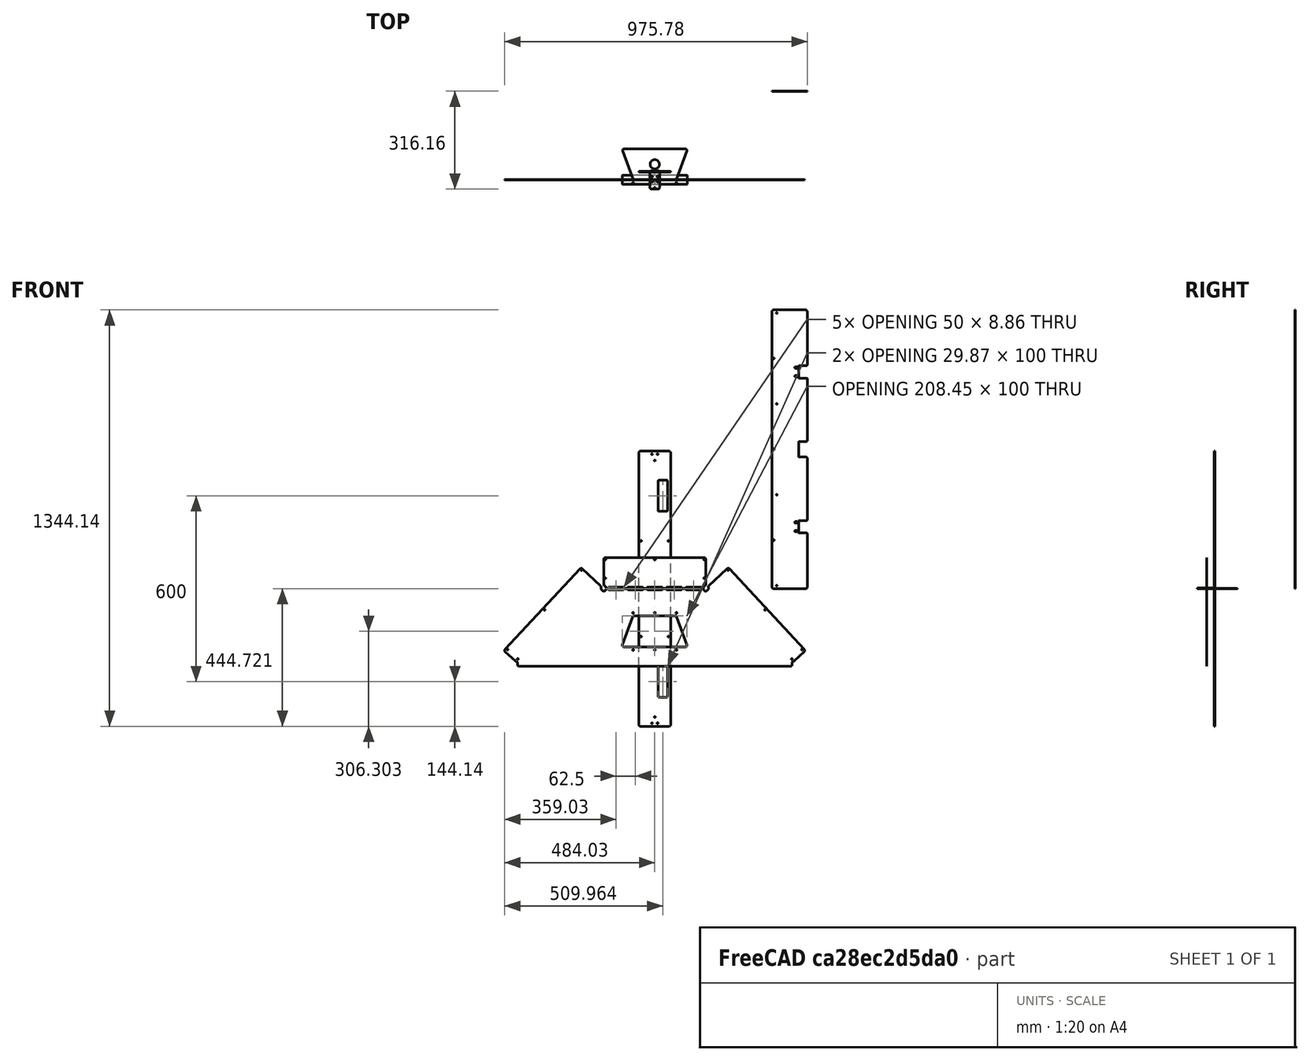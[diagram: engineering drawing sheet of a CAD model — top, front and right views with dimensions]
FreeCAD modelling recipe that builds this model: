
FCSTD DOCUMENT  (FreeCAD 0.22R38622 (Git))
Label: composit_stand12_ss
License: All rights reserved
LicenseURL: http://en.wikipedia.org/wiki/All_rights_reserved
objects: Sketcher::SketchObject×22, TechDraw::DrawViewDimension×16, TechDraw::DrawProjGroupItem×8, App::DocumentObjectGroup×8, Part::Feature×6, App::Link×5, TechDraw::DrawSVGTemplate×4, TechDraw::DrawPage×4, TechDraw::DrawViewBalloon×2
note: 80 computed .brp shape members not serialized (recipe doc carries the construction recipe); baked Part::Feature solids carry a one-line shape summary decoded from their .brp
EXTERNAL_REF file=composit_stand12.FCStd obj=Body008
EXTERNAL_REF file=composit_stand12.FCStd obj=Body002
EXTERNAL_REF file=composit_stand12.FCStd obj=Body006
EXTERNAL_REF file=composit_stand12.FCStd obj=Body018
EXTERNAL_REF file=composit_stand12.FCStd obj=Body019

FEATURE [App::Link] Link001  label="bar_fix"
  LinkedObject = -> <external composit_stand12.FCStd>#Body008
FEATURE [App::Link] Link002  label="sink"
  LinkedObject = -> <external composit_stand12.FCStd>#Body002
FEATURE [App::Link] Link003  label="bar"
  LinkedObject = -> <external composit_stand12.FCStd>#Body006
FEATURE [Part::Feature] Unfold
  shape: bbox 102.3 x 3.402 x 888.3 mm, 40 faces (baked)
FEATURE [Sketcher::SketchObject] Unfold_Sketch_Outline
  ArcFitTolerance = 0
  FullyConstrained = false
  MakeInternals = false
  sketch-geometry (8):
    g0: LineSegment StartX=-444.137 StartY=-46.1681 StartZ=0 EndX=-444.137 EndY=46.1681 EndZ=0
    g1: ArcOfCircle CenterX=-439.137 CenterY=46.1681 CenterZ=0 NormalX=0 NormalY=0 NormalZ=1 AngleXU=1.5708 Radius=5 StartAngle=0 EndAngle=1.5708
    g2: LineSegment StartX=439.137 StartY=51.1681 StartZ=0 EndX=-439.137 EndY=51.1681 EndZ=0
    g3: ArcOfCircle CenterX=439.137 CenterY=46.1681 CenterZ=0 NormalX=0 NormalY=0 NormalZ=1 AngleXU=1.5708 Radius=5 StartAngle=4.71239 EndAngle=6.28319
    g4: LineSegment StartX=444.137 StartY=-46.1681 StartZ=0 EndX=444.137 EndY=46.1681 EndZ=0
    g5: ArcOfCircle CenterX=439.137 CenterY=-46.1681 CenterZ=0 NormalX=0 NormalY=0 NormalZ=1 AngleXU=-1.5708 Radius=5 StartAngle=2e-16 EndAngle=1.5708
    g6: LineSegment StartX=439.137 StartY=-51.1681 StartZ=0 EndX=-439.137 EndY=-51.1681 EndZ=0
    g7: ArcOfCircle CenterX=-439.137 CenterY=-46.1681 CenterZ=0 NormalX=0 NormalY=0 NormalZ=1 AngleXU=-1.5708 Radius=5 StartAngle=4.71239 EndAngle=6.28319
FEATURE [Sketcher::SketchObject] Unfold_Sketch_Internal
  ArcFitTolerance = 0
  FullyConstrained = false
  MakeInternals = false
  sketch-geometry (30):
    g0: ArcOfCircle CenterX=252 CenterY=38.8681 CenterZ=0 NormalX=0 NormalY=0 NormalZ=1 AngleXU=1.5708 Radius=2 StartAngle=4e-16 EndAngle=0.863212
    g1: BSplineCurve PolesCount=15 KnotsCount=13 Degree=3 IsPeriodic=0
    g2: LineSegment StartX=250 StartY=13 StartZ=0 EndX=250 EndY=39.3075 EndZ=0
    g3: ArcOfCircle CenterX=252 CenterY=13 CenterZ=0 NormalX=0 NormalY=0 NormalZ=1 AngleXU=1.5708 Radius=2 StartAngle=1.5708 EndAngle=3.14159
    g4: LineSegment StartX=348 StartY=11 StartZ=0 EndX=252 EndY=11 EndZ=0
    g5: ArcOfCircle CenterX=348 CenterY=13 CenterZ=0 NormalX=0 NormalY=0 NormalZ=1 AngleXU=1.5708 Radius=2 StartAngle=3.14159 EndAngle=4.71239
    g6: LineSegment StartX=350 StartY=39.3075 StartZ=0 EndX=350 EndY=13 EndZ=0
    g7: BSplineCurve PolesCount=15 KnotsCount=13 Degree=3 IsPeriodic=0
    g8: ArcOfCircle CenterX=348 CenterY=38.8681 CenterZ=0 NormalX=0 NormalY=0 NormalZ=1 AngleXU=1.5708 Radius=2 StartAngle=5.41997 EndAngle=6.28319
    g9: LineSegment StartX=348 StartY=40.8681 StartZ=0 EndX=252 EndY=40.8681 EndZ=0
    g10: LineSegment StartX=-350 StartY=13 StartZ=0 EndX=-350 EndY=39.3075 EndZ=0
    g11: BSplineCurve PolesCount=15 KnotsCount=13 Degree=3 IsPeriodic=0
    g12: ArcOfCircle CenterX=-348 CenterY=38.8681 CenterZ=0 NormalX=0 NormalY=0 NormalZ=1 AngleXU=1.5708 Radius=2 StartAngle=4e-16 EndAngle=0.863212
    g13: LineSegment StartX=-252 StartY=40.8681 StartZ=0 EndX=-348 EndY=40.8681 EndZ=0
    g14: ArcOfCircle CenterX=-252 CenterY=38.8681 CenterZ=0 NormalX=0 NormalY=0 NormalZ=1 AngleXU=1.5708 Radius=2 StartAngle=5.41997 EndAngle=6.28319
    g15: BSplineCurve PolesCount=15 KnotsCount=13 Degree=3 IsPeriodic=0
    g16: LineSegment StartX=-250 StartY=13 StartZ=0 EndX=-250 EndY=39.3075 EndZ=0
    g17: ArcOfCircle CenterX=-252 CenterY=13 CenterZ=0 NormalX=0 NormalY=0 NormalZ=1 AngleXU=1.5708 Radius=2 StartAngle=3.14159 EndAngle=4.71239
    g18: LineSegment StartX=-252 StartY=11 StartZ=0 EndX=-348 EndY=11 EndZ=0
    g19: ArcOfCircle CenterX=-348 CenterY=13 CenterZ=0 NormalX=0 NormalY=0 NormalZ=1 AngleXU=1.5708 Radius=2 StartAngle=1.5708 EndAngle=3.14159
    g20: Circle CenterX=414.137 CenterY=0 CenterZ=0 NormalX=0 NormalY=0 NormalZ=-1 AngleXU=-1.5708 Radius=1.7
    g21: Circle CenterX=-414.137 CenterY=0 CenterZ=0 NormalX=0 NormalY=0 NormalZ=-1 AngleXU=1.5708 Radius=1.7
    g22: Circle CenterX=434.137 CenterY=9 CenterZ=0 NormalX=0 NormalY=0 NormalZ=-1 AngleXU=-1.5708 Radius=1.7
    g23: Circle CenterX=-434.137 CenterY=9 CenterZ=0 NormalX=0 NormalY=0 NormalZ=-1 AngleXU=1.5708 Radius=1.7
    g24: Circle CenterX=434.137 CenterY=-9 CenterZ=0 NormalX=0 NormalY=0 NormalZ=-1 AngleXU=-1.5708 Radius=1.7
    g25: Circle CenterX=-434.137 CenterY=-9 CenterZ=0 NormalX=0 NormalY=0 NormalZ=-1 AngleXU=1.5708 Radius=1.7
    g26: Circle CenterX=154.5 CenterY=-44.1681 CenterZ=0 NormalX=0 NormalY=0 NormalZ=1 AngleXU=-3.14159 Radius=1.7
    g27: Circle CenterX=-154.5 CenterY=-44.1681 CenterZ=0 NormalX=0 NormalY=0 NormalZ=1 AngleXU=-3.14159 Radius=1.7
    g28: Circle CenterX=154.5 CenterY=44.1681 CenterZ=0 NormalX=0 NormalY=0 NormalZ=1 AngleXU=-3.14159 Radius=1.7
    g29: Circle CenterX=-154.5 CenterY=44.1681 CenterZ=0 NormalX=0 NormalY=0 NormalZ=1 AngleXU=-3.14159 Radius=1.7
FEATURE [Sketcher::SketchObject] Unfold_Sketch_bends
  ArcFitTolerance = 0
  FullyConstrained = false
  MakeInternals = false
  sketch-geometry (8):
    g0: LineSegment StartX=-444.137 StartY=15.042 StartZ=0 EndX=-350 EndY=15.042 EndZ=0
    g1: LineSegment StartX=-444.137 StartY=38.1261 StartZ=0 EndX=-350 EndY=38.1261 EndZ=0
    g2: LineSegment StartX=-250 StartY=15.042 StartZ=0 EndX=250 EndY=15.042 EndZ=0
    g3: LineSegment StartX=-250 StartY=38.1261 StartZ=0 EndX=250 EndY=38.1261 EndZ=0
    g4: LineSegment StartX=350 StartY=38.1261 StartZ=0 EndX=444.137 EndY=38.1261 EndZ=0
    g5: LineSegment StartX=350 StartY=15.042 StartZ=0 EndX=444.137 EndY=15.042 EndZ=0
    g6: LineSegment StartX=-444.137 StartY=-38.1261 StartZ=0 EndX=444.137 EndY=-38.1261 EndZ=0
    g7: LineSegment StartX=-444.137 StartY=-15.042 StartZ=0 EndX=444.137 EndY=-15.042 EndZ=0
FEATURE [Sketcher::SketchObject] Unfold_Sketch
  ArcFitTolerance = 0
  ExternalGeometry = -> [Unfold_Sketch_bends]
  FullyConstrained = false
  MakeInternals = false
  sketch-geometry (46):
    g0: LineSegment StartX=-444.137 StartY=-46.1681 StartZ=0 EndX=-444.137 EndY=46.1681 EndZ=0
    g1: ArcOfCircle CenterX=-439.137 CenterY=-46.1681 CenterZ=0 NormalX=0 NormalY=0 NormalZ=1 AngleXU=-1.5708 Radius=5 StartAngle=4.71239 EndAngle=6.28319
    g2: LineSegment StartX=439.137 StartY=-51.1681 StartZ=0 EndX=-439.137 EndY=-51.1681 EndZ=0
    g3: ArcOfCircle CenterX=439.137 CenterY=-46.1681 CenterZ=0 NormalX=0 NormalY=0 NormalZ=1 AngleXU=-1.5708 Radius=5 StartAngle=2e-16 EndAngle=1.5708
    g4: LineSegment StartX=444.137 StartY=-46.1681 StartZ=0 EndX=444.137 EndY=46.1681 EndZ=0
    g5: ArcOfCircle CenterX=439.137 CenterY=46.1681 CenterZ=0 NormalX=0 NormalY=0 NormalZ=1 AngleXU=1.5708 Radius=5 StartAngle=4.71239 EndAngle=6.28319
    g6: LineSegment StartX=439.137 StartY=51.1681 StartZ=0 EndX=-439.137 EndY=51.1681 EndZ=0
    g7: ArcOfCircle CenterX=-439.137 CenterY=46.1681 CenterZ=0 NormalX=0 NormalY=0 NormalZ=1 AngleXU=1.5708 Radius=5 StartAngle=0 EndAngle=1.5708
    g8: LineSegment StartX=-350 StartY=13 StartZ=0 EndX=-350 EndY=39.3075 EndZ=0
    g9: BSplineCurve PolesCount=15 KnotsCount=13 Degree=3 IsPeriodic=0
    g10: ArcOfCircle CenterX=-348 CenterY=38.8681 CenterZ=0 NormalX=0 NormalY=0 NormalZ=1 AngleXU=1.5708 Radius=2 StartAngle=4e-16 EndAngle=0.863212
    g11: LineSegment StartX=-252 StartY=40.8681 StartZ=0 EndX=-348 EndY=40.8681 EndZ=0
    g12: ArcOfCircle CenterX=-252 CenterY=38.8681 CenterZ=0 NormalX=0 NormalY=0 NormalZ=1 AngleXU=1.5708 Radius=2 StartAngle=5.41997 EndAngle=6.28319
    g13: BSplineCurve PolesCount=15 KnotsCount=13 Degree=3 IsPeriodic=0
    g14: LineSegment StartX=-250 StartY=13 StartZ=0 EndX=-250 EndY=39.3075 EndZ=0
    g15: ArcOfCircle CenterX=-252 CenterY=13 CenterZ=0 NormalX=0 NormalY=0 NormalZ=1 AngleXU=1.5708 Radius=2 StartAngle=3.14159 EndAngle=4.71239
    g16: LineSegment StartX=-252 StartY=11 StartZ=0 EndX=-348 EndY=11 EndZ=0
    g17: ArcOfCircle CenterX=-348 CenterY=13 CenterZ=0 NormalX=0 NormalY=0 NormalZ=1 AngleXU=1.5708 Radius=2 StartAngle=1.5708 EndAngle=3.14159
    g18: ArcOfCircle CenterX=252 CenterY=38.8681 CenterZ=0 NormalX=0 NormalY=0 NormalZ=1 AngleXU=1.5708 Radius=2 StartAngle=4e-16 EndAngle=0.863212
    g19: LineSegment StartX=348 StartY=40.8681 StartZ=0 EndX=252 EndY=40.8681 EndZ=0
    g20: ArcOfCircle CenterX=348 CenterY=38.8681 CenterZ=0 NormalX=0 NormalY=0 NormalZ=1 AngleXU=1.5708 Radius=2 StartAngle=5.41997 EndAngle=6.28319
    g21: BSplineCurve PolesCount=15 KnotsCount=13 Degree=3 IsPeriodic=0
    g22: LineSegment StartX=350 StartY=39.3075 StartZ=0 EndX=350 EndY=13 EndZ=0
    g23: ArcOfCircle CenterX=348 CenterY=13 CenterZ=0 NormalX=0 NormalY=0 NormalZ=1 AngleXU=1.5708 Radius=2 StartAngle=3.14159 EndAngle=4.71239
    g24: LineSegment StartX=348 StartY=11 StartZ=0 EndX=252 EndY=11 EndZ=0
    g25: ArcOfCircle CenterX=252 CenterY=13 CenterZ=0 NormalX=0 NormalY=0 NormalZ=1 AngleXU=1.5708 Radius=2 StartAngle=1.5708 EndAngle=3.14159
    g26: LineSegment StartX=250 StartY=13 StartZ=0 EndX=250 EndY=39.3075 EndZ=0
    g27: BSplineCurve PolesCount=15 KnotsCount=13 Degree=3 IsPeriodic=0
    g28: Circle CenterX=-154.5 CenterY=44.1681 CenterZ=0 NormalX=0 NormalY=0 NormalZ=1 AngleXU=-3.14159 Radius=1.7
    g29: Circle CenterX=154.5 CenterY=44.1681 CenterZ=0 NormalX=0 NormalY=0 NormalZ=1 AngleXU=-3.14159 Radius=1.7
    g30: Circle CenterX=-154.5 CenterY=-44.1681 CenterZ=0 NormalX=0 NormalY=0 NormalZ=1 AngleXU=-3.14159 Radius=1.7
    g31: Circle CenterX=154.5 CenterY=-44.1681 CenterZ=0 NormalX=0 NormalY=0 NormalZ=1 AngleXU=-3.14159 Radius=1.7
    g32: Circle CenterX=-434.137 CenterY=-9 CenterZ=0 NormalX=0 NormalY=0 NormalZ=-1 AngleXU=1.5708 Radius=1.7
    g33: Circle CenterX=434.137 CenterY=-9 CenterZ=0 NormalX=0 NormalY=0 NormalZ=-1 AngleXU=-1.5708 Radius=1.7
    g34: Circle CenterX=-414.137 CenterY=0 CenterZ=0 NormalX=0 NormalY=0 NormalZ=-1 AngleXU=1.5708 Radius=1.7
    g35: Circle CenterX=-434.137 CenterY=9 CenterZ=0 NormalX=0 NormalY=0 NormalZ=-1 AngleXU=1.5708 Radius=1.7
    g36: Circle CenterX=414.137 CenterY=0 CenterZ=0 NormalX=0 NormalY=0 NormalZ=-1 AngleXU=-1.5708 Radius=1.7
    g37: Circle CenterX=434.137 CenterY=9 CenterZ=0 NormalX=0 NormalY=0 NormalZ=-1 AngleXU=-1.5708 Radius=1.7
    g38: LineSegment StartX=444.137 StartY=38.1261 StartZ=0 EndX=442.137 EndY=38.1261 EndZ=0
    g39: LineSegment StartX=444.137 StartY=15.042 StartZ=0 EndX=442.137 EndY=15.042 EndZ=0
    g40: LineSegment StartX=444.137 StartY=-15.042 StartZ=0 EndX=442.137 EndY=-15.042 EndZ=0
    g41: LineSegment StartX=444.137 StartY=-38.1261 StartZ=0 EndX=442.137 EndY=-38.1261 EndZ=0
    g42: LineSegment StartX=-444.137 StartY=-38.1261 StartZ=0 EndX=-442.137 EndY=-38.1261 EndZ=0
    g43: LineSegment StartX=-444.137 StartY=-15.042 StartZ=0 EndX=-442.137 EndY=-15.042 EndZ=0
    g44: LineSegment StartX=-444.137 StartY=15.042 StartZ=0 EndX=-442.137 EndY=15.042 EndZ=0
    g45: LineSegment StartX=-444.137 StartY=38.1261 StartZ=0 EndX=-442.137 EndY=38.1261 EndZ=0
  constraints (24):
    c: Coincident(g38,g-8)
    c: PointOnObject(g38,g-8)
    c: Coincident(g39,g-7)
    c: PointOnObject(g39,g-7)
    c: Coincident(g40,g-5)
    c: PointOnObject(g40,g-5)
    c: Coincident(g41,g-6)
    c: PointOnObject(g41,g-6)
    c: Coincident(g42,g-6)
    c: PointOnObject(g42,g-6)
    c: Coincident(g43,g-5)
    c: Coincident(g44,g-4)
    c: PointOnObject(g44,g-4)
    c: Coincident(g45,g-3)
    c: PointOnObject(g45,g-3)
    c: PointOnObject(g43,g-5)
    c: Equal(g45,g44)
    c: Equal(g44,g43)
    c: Equal(g43,g42)
    c: Equal(g42,g38)
    c: Equal(g38,g39)
    c: Equal(g39,g40)
    c: Equal(g40,g41)
    c: Distance(g45) = 2
FEATURE [TechDraw::DrawSVGTemplate] Template
  Height = 210
  Orientation = 1
  Template = <path>
  Width = 297
FEATURE [TechDraw::DrawProjGroupItem] View
  CoarseView = false
  Direction = (0,0,1)
  Focus = 100
  HardHidden = false
  IsoCount = 0
  IsoHidden = false
  IsoVisible = false
  LockPosition = false
  Perspective = false
  Rotation = 0
  RotationVector = (1,0,0)
  Scale = 3
  ScaleType = 2
  ScrubCount = 0
  SeamHidden = false
  SeamVisible = true
  SmoothHidden = false
  SmoothVisible = true
  Type = 0
  X = 148.5
  XDirection = (1,0,0)
  XSource = -> [Link003]
  Y = 75
FEATURE [TechDraw::DrawProjGroupItem] View001
  CoarseView = false
  Direction = (0.57735,-0.57735,0.57735)
  Focus = 100
  HardHidden = false
  IsoCount = 0
  IsoHidden = false
  IsoVisible = false
  LockPosition = false
  Perspective = false
  Rotation = 90
  RotationVector = (1,0,0)
  Scale = 0.35
  ScaleType = 2
  ScrubCount = 0
  SeamHidden = false
  SeamVisible = true
  SmoothHidden = false
  SmoothVisible = true
  Type = 0
  X = 148.5
  XDirection = (0.707107,0.707107,0)
  XSource = -> [Link003]
  Y = 185
FEATURE [TechDraw::DrawViewDimension] Dimension003
  AngleOverride = false
  Arbitrary = false
  ArbitraryTolerances = false
  BoxCorners = (2) [(-97.5,-40.5,-1e-07),(97.5,40.5,1e-07)]
  EqualTolerance = true
  ExtensionAngle = 0
  FormatSpec = R%.2w
  FormatSpecOverTolerance = %+.2w
  FormatSpecUnderTolerance = %+.2w
  Inverted = false
  LineAngle = 0
  LockPosition = false
  MeasureType = 1
  OverTolerance = 0
  References2D = -> [View]
  Rotation = 0
  ScaleType = 0
  TheoreticalExact = false
  Type = 4
  UnderTolerance = 0
  X = -73.3131
  Y = -20.44
FEATURE [TechDraw::DrawViewDimension] Dimension004
  AngleOverride = false
  Arbitrary = false
  ArbitraryTolerances = false
  BoxCorners = (2) [(-97.5,-40.5,-1e-07),(97.5,40.5,1e-07)]
  EqualTolerance = true
  ExtensionAngle = 0
  FormatSpec = R%.2w
  FormatSpecOverTolerance = %+.2w
  FormatSpecUnderTolerance = %+.2w
  Inverted = false
  LineAngle = 0
  LockPosition = false
  MeasureType = 1
  OverTolerance = 0
  References2D = -> [View]
  Rotation = 0
  ScaleType = 0
  TheoreticalExact = false
  Type = 4
  UnderTolerance = 0
  X = -35.0129
  Y = 30.8957
FEATURE [TechDraw::DrawSVGTemplate] Template001
  Height = 210
  Orientation = 1
  Template = <path>
  Width = 297
FEATURE [TechDraw::DrawProjGroupItem] View002
  CoarseView = false
  Direction = (0.762766,0.635546,0.119454)
  Focus = 100
  HardHidden = false
  IsoCount = 0
  IsoHidden = false
  IsoVisible = false
  LockPosition = false
  Perspective = false
  Rotation = 0
  RotationVector = (1,0,0)
  Scale = 0.4
  ScaleType = 2
  ScrubCount = 0
  SeamHidden = false
  SeamVisible = true
  SmoothHidden = false
  SmoothVisible = true
  Type = 0
  X = 135.108
  XDirection = (-0.64013,0.768267,3.37444e-07)
  XSource = -> [Link002]
  Y = 41.2296
FEATURE [TechDraw::DrawProjGroupItem] View003
  CoarseView = false
  Direction = (1,0,0)
  Focus = 100
  HardHidden = false
  IsoCount = 0
  IsoHidden = false
  IsoVisible = false
  LockPosition = false
  Perspective = false
  Rotation = 0
  RotationVector = (1,0,0)
  Scale = 0.5
  ScaleType = 2
  ScrubCount = 0
  SeamHidden = false
  SeamVisible = true
  SmoothHidden = false
  SmoothVisible = true
  Type = 0
  X = 68.5
  XDirection = (0,1,0)
  XSource = -> [Link002]
  Y = 175
FEATURE [TechDraw::DrawProjGroupItem] View004
  CoarseView = false
  Direction = (0,1,0)
  Focus = 100
  HardHidden = false
  IsoCount = 0
  IsoHidden = false
  IsoVisible = false
  LockPosition = false
  Perspective = false
  Rotation = 0
  RotationVector = (1,0,0)
  Scale = 0.3
  ScaleType = 2
  ScrubCount = 0
  SeamHidden = false
  SeamVisible = true
  SmoothHidden = false
  SmoothVisible = true
  Type = 0
  X = 148.5
  XDirection = (-1,0,0)
  XSource = -> [Link002]
  Y = 105
FEATURE [Part::Feature] Unfold002
  shape: bbox 31 x 59.08 x 2 mm, 16 faces (baked)
FEATURE [Sketcher::SketchObject] Unfold_Sketch_Outline002
  ArcFitTolerance = 0
  FullyConstrained = false
  MakeInternals = false
  sketch-geometry (8):
    g0: LineSegment StartX=-15.5 StartY=-25.0841 StartZ=0 EndX=-15.5 EndY=24 EndZ=0
    g1: ArcOfCircle CenterX=-10.5 CenterY=24 CenterZ=0 NormalX=0 NormalY=0 NormalZ=1 AngleXU=3.14159 Radius=5 StartAngle=4.71239 EndAngle=6.28319
    g2: LineSegment StartX=-10.5 StartY=29 StartZ=0 EndX=10.5 EndY=29 EndZ=0
    g3: ArcOfCircle CenterX=10.5 CenterY=24 CenterZ=0 NormalX=0 NormalY=0 NormalZ=1 AngleXU=0 Radius=5 StartAngle=0 EndAngle=1.5708
    g4: LineSegment StartX=15.5 StartY=-25.0841 StartZ=0 EndX=15.5 EndY=24 EndZ=0
    g5: ArcOfCircle CenterX=10.5 CenterY=-25.0841 CenterZ=0 NormalX=0 NormalY=0 NormalZ=1 AngleXU=0 Radius=5 StartAngle=4.71239 EndAngle=6.28319
    g6: LineSegment StartX=-10.5 StartY=-30.0841 StartZ=0 EndX=10.5 EndY=-30.0841 EndZ=0
    g7: ArcOfCircle CenterX=-10.5 CenterY=-25.0841 CenterZ=0 NormalX=0 NormalY=0 NormalZ=1 AngleXU=3.14159 Radius=5 StartAngle=2.887e-13 EndAngle=1.5708
FEATURE [Sketcher::SketchObject] Unfold_Sketch_Internal002
  ArcFitTolerance = 0
  FullyConstrained = false
  MakeInternals = false
  sketch-geometry (6):
    g0: Circle CenterX=-9 CenterY=10 CenterZ=0 NormalX=0 NormalY=0 NormalZ=-1 AngleXU=-3.14159 Radius=1.7
    g1: Circle CenterX=9 CenterY=10 CenterZ=0 NormalX=0 NormalY=0 NormalZ=-1 AngleXU=-3.14159 Radius=1.7
    g2: Circle CenterX=-9 CenterY=-6.08407 CenterZ=0 NormalX=0 NormalY=0 NormalZ=-1 AngleXU=-3.14159 Radius=1.7
    g3: Circle CenterX=9 CenterY=-6.08407 CenterZ=0 NormalX=0 NormalY=0 NormalZ=-1 AngleXU=-3.14159 Radius=1.7
    g4: Circle CenterX=0 CenterY=25.5885 CenterZ=0 NormalX=0 NormalY=0 NormalZ=-1 AngleXU=-3.14159 Radius=1.7
    g5: Circle CenterX=0 CenterY=-26.0841 CenterZ=0 NormalX=0 NormalY=0 NormalZ=-1 AngleXU=-3.14159 Radius=1.7
FEATURE [Sketcher::SketchObject] Unfold_Sketch_bends002
  ArcFitTolerance = 0
  FullyConstrained = false
  MakeInternals = false
  Placement = pos=(0,0.00147161,-0.0536581) rot=(1,0,0;0.027419rad)
  sketch-geometry (1):
    g0: LineSegment StartX=15.5 StartY=1.95723 StartZ=0 EndX=-15.5 EndY=1.95723 EndZ=0
FEATURE [Sketcher::SketchObject] Unfold_Sketch002
  ArcFitTolerance = 0
  ExternalGeometry = -> [Unfold_Sketch_bends002]
  FullyConstrained = false
  MakeInternals = false
  sketch-geometry (16):
    g0: LineSegment StartX=-15.5 StartY=-25.0841 StartZ=0 EndX=-15.5 EndY=24 EndZ=0
    g1: ArcOfCircle CenterX=-10.5 CenterY=-25.0841 CenterZ=0 NormalX=0 NormalY=0 NormalZ=1 AngleXU=3.14159 Radius=5 StartAngle=2.887e-13 EndAngle=1.5708
    g2: LineSegment StartX=-10.5 StartY=-30.0841 StartZ=0 EndX=10.5 EndY=-30.0841 EndZ=0
    g3: ArcOfCircle CenterX=10.5 CenterY=-25.0841 CenterZ=0 NormalX=0 NormalY=0 NormalZ=1 AngleXU=0 Radius=5 StartAngle=4.71239 EndAngle=6.28319
    g4: LineSegment StartX=15.5 StartY=-25.0841 StartZ=0 EndX=15.5 EndY=24 EndZ=0
    g5: ArcOfCircle CenterX=10.5 CenterY=24 CenterZ=0 NormalX=0 NormalY=0 NormalZ=1 AngleXU=0 Radius=5 StartAngle=0 EndAngle=1.5708
    g6: LineSegment StartX=-10.5 StartY=29 StartZ=0 EndX=10.5 EndY=29 EndZ=0
    g7: ArcOfCircle CenterX=-10.5 CenterY=24 CenterZ=0 NormalX=0 NormalY=0 NormalZ=1 AngleXU=3.14159 Radius=5 StartAngle=4.71239 EndAngle=6.28319
    g8: Circle CenterX=9 CenterY=-6.08407 CenterZ=0 NormalX=0 NormalY=0 NormalZ=-1 AngleXU=-3.14159 Radius=1.7
    g9: Circle CenterX=-9 CenterY=-6.08407 CenterZ=0 NormalX=0 NormalY=0 NormalZ=-1 AngleXU=-3.14159 Radius=1.7
    g10: Circle CenterX=0 CenterY=-26.0841 CenterZ=0 NormalX=0 NormalY=0 NormalZ=-1 AngleXU=-3.14159 Radius=1.7
    g11: Circle CenterX=0 CenterY=25.5885 CenterZ=0 NormalX=0 NormalY=0 NormalZ=-1 AngleXU=-3.14159 Radius=1.7
    g12: Circle CenterX=9 CenterY=10 CenterZ=0 NormalX=0 NormalY=0 NormalZ=-1 AngleXU=-3.14159 Radius=1.7
    g13: Circle CenterX=-9 CenterY=10 CenterZ=0 NormalX=0 NormalY=0 NormalZ=-1 AngleXU=-3.14159 Radius=1.7
    g14: LineSegment StartX=-15.5 StartY=1.95796 StartZ=0 EndX=-13.5 EndY=1.95796 EndZ=0
    g15: LineSegment StartX=15.5 StartY=1.95796 StartZ=0 EndX=13.5 EndY=1.95796 EndZ=0
  constraints (6):
    c: Coincident(g14,g-3)
    c: PointOnObject(g14,g-3)
    c: Coincident(g15,g-3)
    c: PointOnObject(g15,g-3)
    c: Equal(g14,g15)
    c: Distance(g14) = 2
FEATURE [TechDraw::DrawSVGTemplate] Template002
  Height = 210
  Orientation = 1
  Template = <path>
  Width = 297
FEATURE [TechDraw::DrawProjGroupItem] View005
  CoarseView = false
  Direction = (1,0,0)
  Focus = 100
  HardHidden = false
  IsoCount = 0
  IsoHidden = false
  IsoVisible = false
  LockPosition = false
  Perspective = false
  Rotation = 0
  RotationVector = (1,0,0)
  Scale = 4
  ScaleType = 2
  ScrubCount = 0
  SeamHidden = false
  SeamVisible = true
  SmoothHidden = false
  SmoothVisible = true
  Type = 0
  X = 112.67
  XDirection = (0,1,0)
  XSource = -> [Link001]
  Y = 121.972
FEATURE [TechDraw::DrawViewDimension] Dimension009
  AngleOverride = false
  Arbitrary = false
  ArbitraryTolerances = false
  BoxCorners = (2) [(-58,-68,-1e-07),(58,68,1e-07)]
  EqualTolerance = true
  ExtensionAngle = 0
  FormatSpec = %.2w
  FormatSpecOverTolerance = %+.2w
  FormatSpecUnderTolerance = %+.2w
  Inverted = false
  LineAngle = 0
  LockPosition = false
  MeasureType = 1
  OverTolerance = 0
  References2D = -> [View005]
  Rotation = 0
  ScaleType = 0
  TheoreticalExact = false
  Type = 6
  UnderTolerance = 0
  X = 0
  Y = 2.5
FEATURE [TechDraw::DrawViewDimension] Dimension010
  AngleOverride = false
  Arbitrary = false
  ArbitraryTolerances = false
  BoxCorners = (2) [(-58,-68,-1e-07),(58,68,1e-07)]
  EqualTolerance = true
  ExtensionAngle = 0
  FormatSpec = %.2w
  FormatSpecOverTolerance = %+.2w
  FormatSpecUnderTolerance = %+.2w
  Inverted = false
  LineAngle = 0
  LockPosition = false
  MeasureType = 1
  OverTolerance = 0
  References2D = -> [View005]
  Rotation = 0
  ScaleType = 0
  TheoreticalExact = false
  Type = 1
  UnderTolerance = 0
  X = 0
  Y = -79.2993
FEATURE [TechDraw::DrawViewDimension] Dimension011
  AngleOverride = false
  Arbitrary = false
  ArbitraryTolerances = false
  BoxCorners = (2) [(-58,-68,-1e-07),(58,68,1e-07)]
  EqualTolerance = true
  ExtensionAngle = 0
  FormatSpec = %.2w
  FormatSpecOverTolerance = %+.2w
  FormatSpecUnderTolerance = %+.2w
  Inverted = false
  LineAngle = 0
  LockPosition = false
  MeasureType = 1
  OverTolerance = 0
  References2D = -> [View005]
  Rotation = 0
  ScaleType = 0
  TheoreticalExact = false
  Type = 2
  UnderTolerance = 0
  X = -80.9253
  Y = 4.74458
FEATURE [TechDraw::DrawPage] Page002
  KeepUpdated = true
  NextBalloonIndex = 1
  ProjectionType = 0
  Template = -> Template002
  Views = -> [View005,Dimension009,Dimension010,Dimension011]
FEATURE [App::DocumentObjectGroup] Group004  label="bar_fix_Group"
  Group = -> [Unfold002,Unfold_Sketch002,Unfold_Sketch_Outline002,Unfold_Sketch_Internal002,Unfold_Sketch_bends002,Page002]
FEATURE [Part::Feature] Unfold003
  shape: bbox 113.3 x 0.7 x 900 mm, 57 faces (baked)
FEATURE [Sketcher::SketchObject] Unfold_Sketch003
  ArcFitTolerance = 0
  FullyConstrained = false
  MakeInternals = false
  sketch-geometry (55):
    g0: ArcOfCircle CenterX=-222 CenterY=489.747 CenterZ=0 NormalX=0 NormalY=0 NormalZ=1 AngleXU=-1.5708 Radius=2 StartAngle=1.5708 EndAngle=3.14159
    g1: LineSegment StartX=-222 StartY=491.747 StartZ=0 EndX=-422 EndY=491.747 EndZ=0
    g2: ArcOfCircle CenterX=-422 CenterY=488.747 CenterZ=0 NormalX=0 NormalY=0 NormalZ=1 AngleXU=-1.5708 Radius=3 StartAngle=3.14159 EndAngle=4.71239
    g3: LineSegment StartX=-425 StartY=465.799 StartZ=0 EndX=-425 EndY=488.747 EndZ=0
    g4: ArcOfCircle CenterX=-427 CenterY=465.799 CenterZ=0 NormalX=0 NormalY=0 NormalZ=1 AngleXU=-1.5708 Radius=2 StartAngle=0 EndAngle=1.5708
    g5: LineSegment StartX=-473 StartY=463.799 StartZ=0 EndX=-427 EndY=463.799 EndZ=0
    g6: ArcOfCircle CenterX=-473 CenterY=465.799 CenterZ=0 NormalX=0 NormalY=0 NormalZ=1 AngleXU=-1.5708 Radius=2 StartAngle=4.71239 EndAngle=6.28319
    g7: LineSegment StartX=-475 StartY=465.799 StartZ=0 EndX=-475 EndY=488.747 EndZ=0
    g8: ArcOfCircle CenterX=-478 CenterY=488.747 CenterZ=0 NormalX=0 NormalY=0 NormalZ=1 AngleXU=-1.5708 Radius=3 StartAngle=1.5708 EndAngle=3.14159
    g9: LineSegment StartX=-478 StartY=491.747 StartZ=0 EndX=-678 EndY=491.747 EndZ=0
    g10: ArcOfCircle CenterX=-678 CenterY=489.747 CenterZ=0 NormalX=0 NormalY=0 NormalZ=1 AngleXU=-1.5708 Radius=2 StartAngle=3.14159 EndAngle=4.71239
    g11: LineSegment StartX=-680 StartY=464.756 StartZ=0 EndX=-680 EndY=489.747 EndZ=0
    g12: ArcOfCircle CenterX=-681 CenterY=464.756 CenterZ=0 NormalX=0 NormalY=0 NormalZ=1 AngleXU=-1.5708 Radius=1 StartAngle=0 EndAngle=1.5708
    g13: LineSegment StartX=-719 StartY=463.756 StartZ=0 EndX=-681 EndY=463.756 EndZ=0
    g14: ArcOfCircle CenterX=-719 CenterY=464.756 CenterZ=0 NormalX=0 NormalY=0 NormalZ=1 AngleXU=-1.5708 Radius=1 StartAngle=4.71239 EndAngle=6.28319
    g15: LineSegment StartX=-720 StartY=489.747 StartZ=0 EndX=-720 EndY=464.756 EndZ=0
    g16: ArcOfCircle CenterX=-722 CenterY=489.747 CenterZ=0 NormalX=0 NormalY=0 NormalZ=1 AngleXU=-1.5708 Radius=2 StartAngle=1.5708 EndAngle=3.14159
    g17: LineSegment StartX=-722 StartY=491.747 StartZ=0 EndX=-895 EndY=491.747 EndZ=0
    g18: ArcOfCircle CenterX=-895 CenterY=486.747 CenterZ=0 NormalX=0 NormalY=0 NormalZ=1 AngleXU=-1.5708 Radius=5 StartAngle=3.14159 EndAngle=4.71239
    g19: LineSegment StartX=-900 StartY=486.747 StartZ=0 EndX=-900 EndY=383.437 EndZ=0
    g20: ArcOfCircle CenterX=-895 CenterY=383.437 CenterZ=0 NormalX=0 NormalY=0 NormalZ=1 AngleXU=1.5708 Radius=5 StartAngle=1.5708 EndAngle=3.14159
    g21: LineSegment StartX=-5 StartY=378.437 StartZ=0 EndX=-895 EndY=378.437 EndZ=0
    g22: ArcOfCircle CenterX=-5 CenterY=383.437 CenterZ=0 NormalX=0 NormalY=0 NormalZ=1 AngleXU=1.5708 Radius=5 StartAngle=3.14159 EndAngle=4.71239
    g23: LineSegment StartX=0 StartY=486.747 StartZ=0 EndX=0 EndY=383.437 EndZ=0
    g24: ArcOfCircle CenterX=-5 CenterY=486.747 CenterZ=0 NormalX=0 NormalY=0 NormalZ=1 AngleXU=-1.5708 Radius=5 StartAngle=1.5708 EndAngle=3.14159
    g25: LineSegment StartX=-5 StartY=491.747 StartZ=0 EndX=-178 EndY=491.747 EndZ=0
    g26: ArcOfCircle CenterX=-178 CenterY=489.747 CenterZ=0 NormalX=0 NormalY=0 NormalZ=1 AngleXU=-1.5708 Radius=2 StartAngle=3.14159 EndAngle=4.71239
    g27: LineSegment StartX=-180 StartY=464.756 StartZ=0 EndX=-180 EndY=489.747 EndZ=0
    g28: ArcOfCircle CenterX=-181 CenterY=464.756 CenterZ=0 NormalX=0 NormalY=0 NormalZ=1 AngleXU=-1.5708 Radius=1 StartAngle=0 EndAngle=1.5708
    g29: LineSegment StartX=-219 StartY=463.756 StartZ=0 EndX=-181 EndY=463.756 EndZ=0
    g30: ArcOfCircle CenterX=-219 CenterY=464.756 CenterZ=0 NormalX=0 NormalY=0 NormalZ=1 AngleXU=-1.5708 Radius=1 StartAngle=4.71239 EndAngle=6.28319
    g31: LineSegment StartX=-220 StartY=489.747 StartZ=0 EndX=-220 EndY=464.756 EndZ=0
    g32: LineSegment StartX=-716.5 StartY=453.756 StartZ=0 EndX=-716.5 EndY=458.756 EndZ=0
    g33: ArcOfCircle CenterX=-714 CenterY=458.756 CenterZ=0 NormalX=0 NormalY=0 NormalZ=1 AngleXU=-1.5708 Radius=2.5 StartAngle=1.5708 EndAngle=4.71239
    g34: LineSegment StartX=-711.5 StartY=453.756 StartZ=0 EndX=-711.5 EndY=458.756 EndZ=0
    g35: ArcOfCircle CenterX=-714 CenterY=453.756 CenterZ=0 NormalX=0 NormalY=0 NormalZ=1 AngleXU=-1.5708 Radius=2.5 StartAngle=4.71239 EndAngle=7.85398
    g36: LineSegment StartX=-688.5 StartY=453.756 StartZ=0 EndX=-688.5 EndY=458.756 EndZ=0
    g37: ArcOfCircle CenterX=-686 CenterY=458.756 CenterZ=0 NormalX=0 NormalY=0 NormalZ=1 AngleXU=-1.5708 Radius=2.5 StartAngle=1.5708 EndAngle=4.71239
    g38: LineSegment StartX=-683.5 StartY=453.756 StartZ=0 EndX=-683.5 EndY=458.756 EndZ=0
    g39: ArcOfCircle CenterX=-686 CenterY=453.756 CenterZ=0 NormalX=0 NormalY=0 NormalZ=1 AngleXU=-1.5708 Radius=2.5 StartAngle=4.71239 EndAngle=7.85398
    g40: LineSegment StartX=-216.5 StartY=453.756 StartZ=0 EndX=-216.5 EndY=458.756 EndZ=0
    g41: ArcOfCircle CenterX=-214 CenterY=458.756 CenterZ=0 NormalX=0 NormalY=0 NormalZ=1 AngleXU=-1.5708 Radius=2.5 StartAngle=1.5708 EndAngle=4.71239
    g42: LineSegment StartX=-211.5 StartY=453.756 StartZ=0 EndX=-211.5 EndY=458.756 EndZ=0
    g43: ArcOfCircle CenterX=-214 CenterY=453.756 CenterZ=0 NormalX=0 NormalY=0 NormalZ=1 AngleXU=-1.5708 Radius=2.5 StartAngle=4.71239 EndAngle=7.85398
    g44: LineSegment StartX=-188.5 StartY=453.756 StartZ=0 EndX=-188.5 EndY=458.756 EndZ=0
    g45: ArcOfCircle CenterX=-186 CenterY=458.756 CenterZ=0 NormalX=0 NormalY=0 NormalZ=1 AngleXU=-1.5708 Radius=2.5 StartAngle=1.5708 EndAngle=4.71239
    g46: LineSegment StartX=-183.5 StartY=453.756 StartZ=0 EndX=-183.5 EndY=458.756 EndZ=0
    g47: ArcOfCircle CenterX=-186 CenterY=453.756 CenterZ=0 NormalX=0 NormalY=0 NormalZ=1 AngleXU=-1.5708 Radius=2.5 StartAngle=4.71239 EndAngle=7.85398
    g48: Circle CenterX=-890 CenterY=393.437 CenterZ=0 NormalX=0 NormalY=0 NormalZ=-1 AngleXU=0 Radius=1.7
    g49: Circle CenterX=-596.667 CenterY=393.437 CenterZ=0 NormalX=0 NormalY=0 NormalZ=-1 AngleXU=0 Radius=1.7
    g50: Circle CenterX=-743.333 CenterY=383.437 CenterZ=0 NormalX=0 NormalY=0 NormalZ=-1 AngleXU=0 Radius=1.7
    g51: Circle CenterX=-10 CenterY=393.437 CenterZ=0 NormalX=0 NormalY=0 NormalZ=-1 AngleXU=0 Radius=1.7
    g52: Circle CenterX=-303.333 CenterY=393.437 CenterZ=0 NormalX=0 NormalY=0 NormalZ=-1 AngleXU=0 Radius=1.7
    g53: Circle CenterX=-450 CenterY=383.437 CenterZ=0 NormalX=0 NormalY=0 NormalZ=-1 AngleXU=0 Radius=1.7
    g54: Circle CenterX=-156.667 CenterY=383.437 CenterZ=0 NormalX=0 NormalY=0 NormalZ=-1 AngleXU=0 Radius=1.7
FEATURE [Sketcher::SketchObject] Unfold_Sketch_Outline003
  ArcFitTolerance = 0
  FullyConstrained = false
  MakeInternals = false
  sketch-geometry (32):
    g0: ArcOfCircle CenterX=-222 CenterY=489.747 CenterZ=0 NormalX=0 NormalY=0 NormalZ=1 AngleXU=-1.5708 Radius=2 StartAngle=1.5708 EndAngle=3.14159
    g1: LineSegment StartX=-222 StartY=491.747 StartZ=0 EndX=-422 EndY=491.747 EndZ=0
    g2: ArcOfCircle CenterX=-422 CenterY=488.747 CenterZ=0 NormalX=0 NormalY=0 NormalZ=1 AngleXU=-1.5708 Radius=3 StartAngle=3.14159 EndAngle=4.71239
    g3: LineSegment StartX=-425 StartY=465.799 StartZ=0 EndX=-425 EndY=488.747 EndZ=0
    g4: ArcOfCircle CenterX=-427 CenterY=465.799 CenterZ=0 NormalX=0 NormalY=0 NormalZ=1 AngleXU=-1.5708 Radius=2 StartAngle=0 EndAngle=1.5708
    g5: LineSegment StartX=-473 StartY=463.799 StartZ=0 EndX=-427 EndY=463.799 EndZ=0
    g6: ArcOfCircle CenterX=-473 CenterY=465.799 CenterZ=0 NormalX=0 NormalY=0 NormalZ=1 AngleXU=-1.5708 Radius=2 StartAngle=4.71239 EndAngle=6.28319
    g7: LineSegment StartX=-475 StartY=465.799 StartZ=0 EndX=-475 EndY=488.747 EndZ=0
    g8: ArcOfCircle CenterX=-478 CenterY=488.747 CenterZ=0 NormalX=0 NormalY=0 NormalZ=1 AngleXU=-1.5708 Radius=3 StartAngle=1.5708 EndAngle=3.14159
    g9: LineSegment StartX=-478 StartY=491.747 StartZ=0 EndX=-678 EndY=491.747 EndZ=0
    g10: ArcOfCircle CenterX=-678 CenterY=489.747 CenterZ=0 NormalX=0 NormalY=0 NormalZ=1 AngleXU=-1.5708 Radius=2 StartAngle=3.14159 EndAngle=4.71239
    g11: LineSegment StartX=-680 StartY=464.756 StartZ=0 EndX=-680 EndY=489.747 EndZ=0
    g12: ArcOfCircle CenterX=-681 CenterY=464.756 CenterZ=0 NormalX=0 NormalY=0 NormalZ=1 AngleXU=-1.5708 Radius=1 StartAngle=0 EndAngle=1.5708
    g13: LineSegment StartX=-719 StartY=463.756 StartZ=0 EndX=-681 EndY=463.756 EndZ=0
    g14: ArcOfCircle CenterX=-719 CenterY=464.756 CenterZ=0 NormalX=0 NormalY=0 NormalZ=1 AngleXU=-1.5708 Radius=1 StartAngle=4.71239 EndAngle=6.28319
    g15: LineSegment StartX=-720 StartY=489.747 StartZ=0 EndX=-720 EndY=464.756 EndZ=0
    g16: ArcOfCircle CenterX=-722 CenterY=489.747 CenterZ=0 NormalX=0 NormalY=0 NormalZ=1 AngleXU=-1.5708 Radius=2 StartAngle=1.5708 EndAngle=3.14159
    g17: LineSegment StartX=-722 StartY=491.747 StartZ=0 EndX=-895 EndY=491.747 EndZ=0
    g18: ArcOfCircle CenterX=-895 CenterY=486.747 CenterZ=0 NormalX=0 NormalY=0 NormalZ=1 AngleXU=-1.5708 Radius=5 StartAngle=3.14159 EndAngle=4.71239
    g19: LineSegment StartX=-900 StartY=486.747 StartZ=0 EndX=-900 EndY=383.437 EndZ=0
    g20: ArcOfCircle CenterX=-895 CenterY=383.437 CenterZ=0 NormalX=0 NormalY=0 NormalZ=1 AngleXU=1.5708 Radius=5 StartAngle=1.5708 EndAngle=3.14159
    g21: LineSegment StartX=-5 StartY=378.437 StartZ=0 EndX=-895 EndY=378.437 EndZ=0
    g22: ArcOfCircle CenterX=-5 CenterY=383.437 CenterZ=0 NormalX=0 NormalY=0 NormalZ=1 AngleXU=1.5708 Radius=5 StartAngle=3.14159 EndAngle=4.71239
    g23: LineSegment StartX=0 StartY=486.747 StartZ=0 EndX=0 EndY=383.437 EndZ=0
    g24: ArcOfCircle CenterX=-5 CenterY=486.747 CenterZ=0 NormalX=0 NormalY=0 NormalZ=1 AngleXU=-1.5708 Radius=5 StartAngle=1.5708 EndAngle=3.14159
    g25: LineSegment StartX=-5 StartY=491.747 StartZ=0 EndX=-178 EndY=491.747 EndZ=0
    g26: ArcOfCircle CenterX=-178 CenterY=489.747 CenterZ=0 NormalX=0 NormalY=0 NormalZ=1 AngleXU=-1.5708 Radius=2 StartAngle=3.14159 EndAngle=4.71239
    g27: LineSegment StartX=-180 StartY=464.756 StartZ=0 EndX=-180 EndY=489.747 EndZ=0
    g28: ArcOfCircle CenterX=-181 CenterY=464.756 CenterZ=0 NormalX=0 NormalY=0 NormalZ=1 AngleXU=-1.5708 Radius=1 StartAngle=0 EndAngle=1.5708
    g29: LineSegment StartX=-219 StartY=463.756 StartZ=0 EndX=-181 EndY=463.756 EndZ=0
    g30: ArcOfCircle CenterX=-219 CenterY=464.756 CenterZ=0 NormalX=0 NormalY=0 NormalZ=1 AngleXU=-1.5708 Radius=1 StartAngle=4.71239 EndAngle=6.28319
    g31: LineSegment StartX=-220 StartY=489.747 StartZ=0 EndX=-220 EndY=464.756 EndZ=0
FEATURE [Sketcher::SketchObject] Unfold_Sketch_Internal003
  ArcFitTolerance = 0
  FullyConstrained = false
  MakeInternals = false
  sketch-geometry (23):
    g0: LineSegment StartX=-188.5 StartY=453.756 StartZ=0 EndX=-188.5 EndY=458.756 EndZ=0
    g1: ArcOfCircle CenterX=-186 CenterY=458.756 CenterZ=0 NormalX=0 NormalY=0 NormalZ=1 AngleXU=-1.5708 Radius=2.5 StartAngle=1.5708 EndAngle=4.71239
    g2: LineSegment StartX=-183.5 StartY=453.756 StartZ=0 EndX=-183.5 EndY=458.756 EndZ=0
    g3: ArcOfCircle CenterX=-186 CenterY=453.756 CenterZ=0 NormalX=0 NormalY=0 NormalZ=1 AngleXU=-1.5708 Radius=2.5 StartAngle=4.71239 EndAngle=7.85398
    g4: LineSegment StartX=-216.5 StartY=453.756 StartZ=0 EndX=-216.5 EndY=458.756 EndZ=0
    g5: ArcOfCircle CenterX=-214 CenterY=458.756 CenterZ=0 NormalX=0 NormalY=0 NormalZ=1 AngleXU=-1.5708 Radius=2.5 StartAngle=1.5708 EndAngle=4.71239
    g6: LineSegment StartX=-211.5 StartY=453.756 StartZ=0 EndX=-211.5 EndY=458.756 EndZ=0
    g7: ArcOfCircle CenterX=-214 CenterY=453.756 CenterZ=0 NormalX=0 NormalY=0 NormalZ=1 AngleXU=-1.5708 Radius=2.5 StartAngle=4.71239 EndAngle=7.85398
    g8: LineSegment StartX=-688.5 StartY=453.756 StartZ=0 EndX=-688.5 EndY=458.756 EndZ=0
    g9: ArcOfCircle CenterX=-686 CenterY=458.756 CenterZ=0 NormalX=0 NormalY=0 NormalZ=1 AngleXU=-1.5708 Radius=2.5 StartAngle=1.5708 EndAngle=4.71239
    g10: LineSegment StartX=-683.5 StartY=453.756 StartZ=0 EndX=-683.5 EndY=458.756 EndZ=0
    g11: ArcOfCircle CenterX=-686 CenterY=453.756 CenterZ=0 NormalX=0 NormalY=0 NormalZ=1 AngleXU=-1.5708 Radius=2.5 StartAngle=4.71239 EndAngle=7.85398
    g12: LineSegment StartX=-716.5 StartY=453.756 StartZ=0 EndX=-716.5 EndY=458.756 EndZ=0
    g13: ArcOfCircle CenterX=-714 CenterY=458.756 CenterZ=0 NormalX=0 NormalY=0 NormalZ=1 AngleXU=-1.5708 Radius=2.5 StartAngle=1.5708 EndAngle=4.71239
    g14: LineSegment StartX=-711.5 StartY=453.756 StartZ=0 EndX=-711.5 EndY=458.756 EndZ=0
    g15: ArcOfCircle CenterX=-714 CenterY=453.756 CenterZ=0 NormalX=0 NormalY=0 NormalZ=1 AngleXU=-1.5708 Radius=2.5 StartAngle=4.71239 EndAngle=7.85398
    g16: Circle CenterX=-743.333 CenterY=383.437 CenterZ=0 NormalX=0 NormalY=0 NormalZ=-1 AngleXU=0 Radius=1.7
    g17: Circle CenterX=-596.667 CenterY=393.437 CenterZ=0 NormalX=0 NormalY=0 NormalZ=-1 AngleXU=0 Radius=1.7
    g18: Circle CenterX=-890 CenterY=393.437 CenterZ=0 NormalX=0 NormalY=0 NormalZ=-1 AngleXU=0 Radius=1.7
    g19: Circle CenterX=-10 CenterY=393.437 CenterZ=0 NormalX=0 NormalY=0 NormalZ=-1 AngleXU=0 Radius=1.7
    g20: Circle CenterX=-156.667 CenterY=383.437 CenterZ=0 NormalX=0 NormalY=0 NormalZ=-1 AngleXU=0 Radius=1.7
    g21: Circle CenterX=-450 CenterY=383.437 CenterZ=0 NormalX=0 NormalY=0 NormalZ=-1 AngleXU=0 Radius=1.7
    g22: Circle CenterX=-303.333 CenterY=393.437 CenterZ=0 NormalX=0 NormalY=0 NormalZ=-1 AngleXU=0 Radius=1.7
FEATURE [Sketcher::SketchObject] Unfold_Sketch_bends003
  ArcFitTolerance = 0
  FullyConstrained = false
  MakeInternals = false
  sketch-geometry (5):
    g0: LineSegment StartX=-425 StartY=467.752 StartZ=0 EndX=-220 EndY=467.752 EndZ=0
    g1: LineSegment StartX=-180 StartY=467.752 StartZ=0 EndX=0 EndY=467.752 EndZ=0
    g2: LineSegment StartX=-900 StartY=467.752 StartZ=0 EndX=-720 EndY=467.752 EndZ=0
    g3: LineSegment StartX=-680 StartY=467.752 StartZ=0 EndX=-475 EndY=467.752 EndZ=0
    g4: LineSegment StartX=-900 StartY=398.241 StartZ=0 EndX=0 EndY=398.241 EndZ=0
FEATURE [TechDraw::DrawSVGTemplate] Template003
  Height = 210
  Orientation = 1
  Template = <path>
  Width = 297
FEATURE [TechDraw::DrawProjGroupItem] View006
  CoarseView = false
  Direction = (0,0,1)
  Focus = 100
  HardHidden = false
  IsoCount = 0
  IsoHidden = false
  IsoVisible = false
  LockPosition = false
  Perspective = false
  Rotation = 0
  RotationVector = (1,0,0)
  ScaleType = 0
  ScrubCount = 0
  SeamHidden = false
  SeamVisible = true
  SmoothHidden = false
  SmoothVisible = true
  Type = 0
  X = 148.5
  XDirection = (1,0,0)
  Y = 105
FEATURE [TechDraw::DrawProjGroupItem] View007
  CoarseView = false
  Direction = (0,0.707107,0.707107)
  Focus = 100
  HardHidden = false
  IsoCount = 0
  IsoHidden = false
  IsoVisible = false
  LockPosition = false
  Perspective = false
  Rotation = 0
  RotationVector = (1,0,0)
  Scale = 0.25
  ScaleType = 2
  ScrubCount = 0
  SeamHidden = false
  SeamVisible = true
  SmoothHidden = false
  SmoothVisible = true
  Type = 0
  X = 68.5
  XDirection = (-1,0,0)
  Y = 105
  expr: Scale = 0.25
FEATURE [TechDraw::DrawViewDimension] Dimension012
  AngleOverride = false
  Arbitrary = false
  ArbitraryTolerances = false
  BoxCorners = (2) [(-34.35,-33.0016,-1e-07),(34.35,33.0016,1e-07)]
  EqualTolerance = true
  ExtensionAngle = 0
  FormatSpec = %.2w
  FormatSpecOverTolerance = %+.2w
  FormatSpecUnderTolerance = %+.2w
  Inverted = false
  LineAngle = 0
  LockPosition = false
  MeasureType = 1
  OverTolerance = 0
  References2D = -> [View006]
  Rotation = 0
  ScaleType = 0
  TheoreticalExact = false
  Type = 6
  UnderTolerance = 0
  X = 0
  Y = 2.5
FEATURE [TechDraw::DrawViewDimension] Dimension013
  AngleOverride = false
  Arbitrary = false
  ArbitraryTolerances = false
  BoxCorners = (2) [(-34.35,-33.0016,-1e-07),(34.35,33.0016,1e-07)]
  EqualTolerance = true
  ExtensionAngle = 0
  FormatSpec = %.2w
  FormatSpecOverTolerance = %+.2w
  FormatSpecUnderTolerance = %+.2w
  Inverted = false
  LineAngle = 0
  LockPosition = false
  MeasureType = 1
  OverTolerance = 0
  References2D = -> [View006]
  Rotation = 0
  ScaleType = 0
  TheoreticalExact = false
  Type = 6
  UnderTolerance = 0
  X = -15.7028
  Y = 23.7449
FEATURE [TechDraw::DrawViewDimension] Dimension014
  AngleOverride = false
  Arbitrary = false
  ArbitraryTolerances = false
  BoxCorners = (2) [(-34.35,-33.0016,-1e-07),(34.35,33.0016,1e-07)]
  EqualTolerance = true
  ExtensionAngle = 0
  FormatSpec = %.2w
  FormatSpecOverTolerance = %+.2w
  FormatSpecUnderTolerance = %+.2w
  Inverted = false
  LineAngle = 0
  LockPosition = false
  MeasureType = 1
  OverTolerance = 0
  References2D = -> [View006]
  Rotation = 0
  ScaleType = 0
  TheoreticalExact = false
  Type = 0
  UnderTolerance = 0
  X = 28.2758
  Y = -26.2152
FEATURE [TechDraw::DrawViewDimension] Dimension015
  AngleOverride = false
  Arbitrary = false
  ArbitraryTolerances = false
  BoxCorners = (2) [(-34.35,-33.0016,-1e-07),(34.35,33.0016,1e-07)]
  EqualTolerance = true
  ExtensionAngle = 0
  FormatSpec = %.2w
  FormatSpecOverTolerance = %+.2w
  FormatSpecUnderTolerance = %+.2w
  Inverted = false
  LineAngle = 0
  LockPosition = false
  MeasureType = 1
  OverTolerance = 0
  References2D = -> [View006]
  Rotation = 0
  ScaleType = 0
  TheoreticalExact = false
  Type = 0
  UnderTolerance = 0
  X = -24.8153
  Y = 44.8075
FEATURE [TechDraw::DrawViewDimension] Dimension016
  AngleOverride = false
  Arbitrary = false
  ArbitraryTolerances = false
  BoxCorners = (2) [(-34.35,-33.0016,-1e-07),(34.35,33.0016,1e-07)]
  EqualTolerance = true
  ExtensionAngle = 0
  FormatSpec = %.2w
  FormatSpecOverTolerance = %+.2w
  FormatSpecUnderTolerance = %+.2w
  Inverted = false
  LineAngle = 0
  LockPosition = false
  MeasureType = 1
  OverTolerance = 0
  References2D = -> [View006]
  Rotation = 0
  ScaleType = 0
  TheoreticalExact = false
  Type = 0
  UnderTolerance = 0
  X = 21.2011
  Y = 16.5945
FEATURE [TechDraw::DrawPage] Page003
  KeepUpdated = true
  NextBalloonIndex = 1
  ProjectionType = 0
  Template = -> Template003
  Views = -> [View006,View007,Dimension012,Dimension013,Dimension014,Dimension015,Dimension016]
FEATURE [App::DocumentObjectGroup] Group005  label="door_ss_Group"
  Group = -> [Unfold003,Unfold_Sketch003,Unfold_Sketch_Outline003,Unfold_Sketch_Internal003,Unfold_Sketch_bends003,Page003]
FEATURE [App::Link] Link  label="sink_cutout"
  LinkedObject = -> <external composit_stand12.FCStd>#Body018
FEATURE [App::Link] Link004  label="sink_jumb"
  LinkedObject = -> <external composit_stand12.FCStd>#Body019
FEATURE [App::DocumentObjectGroup] Group  label="parts"
  Group = -> [Link003,Link001,Link002,Link,Link004]
FEATURE [Part::Feature] Unfold004
  shape: bbox 210 x 30 x 0.7 mm, 13 faces (baked)
FEATURE [Sketcher::SketchObject] Unfold_Sketch004
  ArcFitTolerance = 1e-06
  FullyConstrained = false
  MakeInternals = false
  sketch-geometry (11):
    g0: LineSegment StartX=-103 StartY=-15 StartZ=0 EndX=103 EndY=-15 EndZ=0
    g1: ArcOfCircle CenterX=-103 CenterY=-13 CenterZ=0 NormalX=0 NormalY=0 NormalZ=1 AngleXU=0 Radius=2 StartAngle=3.14159 EndAngle=4.71239
    g2: ArcOfCircle CenterX=103 CenterY=-13 CenterZ=0 NormalX=0 NormalY=0 NormalZ=1 AngleXU=0 Radius=2 StartAngle=4.71239 EndAngle=6.28319
    g3: LineSegment StartX=-105 StartY=13 StartZ=0 EndX=-105 EndY=-13 EndZ=0
    g4: LineSegment StartX=105 StartY=-13 StartZ=0 EndX=105 EndY=13 EndZ=0
    g5: ArcOfCircle CenterX=-103 CenterY=13 CenterZ=0 NormalX=0 NormalY=0 NormalZ=1 AngleXU=0 Radius=2 StartAngle=1.5708 EndAngle=3.14159
    g6: ArcOfCircle CenterX=103 CenterY=13 CenterZ=0 NormalX=0 NormalY=0 NormalZ=1 AngleXU=0 Radius=2 StartAngle=0 EndAngle=1.5708
    g7: LineSegment StartX=103 StartY=15 StartZ=0 EndX=-103 EndY=15 EndZ=0
    g8: Circle CenterX=-70 CenterY=-10 CenterZ=0 NormalX=0 NormalY=0 NormalZ=1 AngleXU=0 Radius=1.7
    g9: Circle CenterX=0 CenterY=-10 CenterZ=0 NormalX=0 NormalY=0 NormalZ=1 AngleXU=0 Radius=1.7
    g10: Circle CenterX=70 CenterY=-10 CenterZ=0 NormalX=0 NormalY=0 NormalZ=1 AngleXU=0 Radius=1.7
FEATURE [Sketcher::SketchObject] Unfold_Sketch_Outline004
  ArcFitTolerance = 1e-06
  FullyConstrained = false
  MakeInternals = false
  sketch-geometry (8):
    g0: LineSegment StartX=-103 StartY=-15 StartZ=0 EndX=103 EndY=-15 EndZ=0
    g1: ArcOfCircle CenterX=103 CenterY=-13 CenterZ=0 NormalX=0 NormalY=0 NormalZ=1 AngleXU=0 Radius=2 StartAngle=4.71239 EndAngle=6.28319
    g2: LineSegment StartX=105 StartY=-13 StartZ=0 EndX=105 EndY=13 EndZ=0
    g3: ArcOfCircle CenterX=103 CenterY=13 CenterZ=0 NormalX=0 NormalY=0 NormalZ=1 AngleXU=0 Radius=2 StartAngle=0 EndAngle=1.5708
    g4: LineSegment StartX=103 StartY=15 StartZ=0 EndX=-103 EndY=15 EndZ=0
    g5: ArcOfCircle CenterX=-103 CenterY=13 CenterZ=0 NormalX=0 NormalY=0 NormalZ=1 AngleXU=0 Radius=2 StartAngle=1.5708 EndAngle=3.14159
    g6: LineSegment StartX=-105 StartY=13 StartZ=0 EndX=-105 EndY=-13 EndZ=0
    g7: ArcOfCircle CenterX=-103 CenterY=-13 CenterZ=0 NormalX=0 NormalY=0 NormalZ=1 AngleXU=0 Radius=2 StartAngle=3.14159 EndAngle=4.71239
FEATURE [Sketcher::SketchObject] Unfold_Sketch_Internal004
  ArcFitTolerance = 1e-06
  FullyConstrained = false
  MakeInternals = false
  sketch-geometry (3):
    g0: Circle CenterX=70 CenterY=-10 CenterZ=0 NormalX=0 NormalY=0 NormalZ=1 AngleXU=0 Radius=1.7
    g1: Circle CenterX=-70 CenterY=-10 CenterZ=0 NormalX=0 NormalY=0 NormalZ=1 AngleXU=0 Radius=1.7
    g2: Circle CenterX=0 CenterY=-10 CenterZ=0 NormalX=0 NormalY=0 NormalZ=1 AngleXU=0 Radius=1.7
FEATURE [App::DocumentObjectGroup] Group006  label="sink_jumb_Group"
  Group = -> [Unfold004,Unfold_Sketch004,Unfold_Sketch_Outline004,Unfold_Sketch_Internal004]
FEATURE [Part::Feature] Unfold005
  shape: bbox 207.5 x 99 x 1.5 mm, 11 faces (baked)
FEATURE [Sketcher::SketchObject] Unfold_Sketch005
  ArcFitTolerance = 1e-06
  FullyConstrained = false
  MakeInternals = false
  sketch-geometry (9):
    g0: ArcOfCircle CenterX=99.2563 CenterY=95 CenterZ=0 NormalX=0 NormalY=0 NormalZ=1 AngleXU=0 Radius=4.5 StartAngle=5.93412 EndAngle=7.85398
    g1: LineSegment StartX=-99.2563 StartY=99.5 StartZ=0 EndX=99.2563 EndY=99.5 EndZ=0
    g2: LineSegment StartX=103.485 StartY=93.4609 StartZ=0 EndX=70.7276 EndY=3.46091 EndZ=0
    g3: ArcOfCircle CenterX=66.499 CenterY=5 CenterZ=0 NormalX=0 NormalY=0 NormalZ=1 AngleXU=0 Radius=4.5 StartAngle=4.71239 EndAngle=5.93412
    g4: ArcOfCircle CenterX=-99.2563 CenterY=95 CenterZ=0 NormalX=0 NormalY=0 NormalZ=1 AngleXU=-3.14159 Radius=4.5 StartAngle=4.71239 EndAngle=6.63225
    g5: LineSegment StartX=-70.7276 StartY=3.46091 StartZ=0 EndX=-103.485 EndY=93.4609 EndZ=0
    g6: LineSegment StartX=66.499 StartY=0.5 StartZ=0 EndX=-66.499 EndY=0.5 EndZ=0
    g7: ArcOfCircle CenterX=-66.499 CenterY=5 CenterZ=0 NormalX=0 NormalY=0 NormalZ=1 AngleXU=-3.14159 Radius=4.5 StartAngle=0.349066 EndAngle=1.5708
    g8: Circle CenterX=0 CenterY=50 CenterZ=0 NormalX=0 NormalY=0 NormalZ=-1 AngleXU=0 Radius=15
FEATURE [Sketcher::SketchObject] Unfold_Sketch_Outline005
  ArcFitTolerance = 1e-06
  FullyConstrained = false
  MakeInternals = false
  sketch-geometry (8):
    g0: ArcOfCircle CenterX=99.2563 CenterY=95 CenterZ=0 NormalX=0 NormalY=0 NormalZ=1 AngleXU=0 Radius=4.5 StartAngle=5.93412 EndAngle=7.85398
    g1: LineSegment StartX=-99.2563 StartY=99.5 StartZ=0 EndX=99.2563 EndY=99.5 EndZ=0
    g2: ArcOfCircle CenterX=-99.2563 CenterY=95 CenterZ=0 NormalX=0 NormalY=0 NormalZ=1 AngleXU=-3.14159 Radius=4.5 StartAngle=4.71239 EndAngle=6.63225
    g3: LineSegment StartX=-70.7276 StartY=3.46091 StartZ=0 EndX=-103.485 EndY=93.4609 EndZ=0
    g4: ArcOfCircle CenterX=-66.499 CenterY=5 CenterZ=0 NormalX=0 NormalY=0 NormalZ=1 AngleXU=-3.14159 Radius=4.5 StartAngle=0.349066 EndAngle=1.5708
    g5: LineSegment StartX=66.499 StartY=0.5 StartZ=0 EndX=-66.499 EndY=0.5 EndZ=0
    g6: ArcOfCircle CenterX=66.499 CenterY=5 CenterZ=0 NormalX=0 NormalY=0 NormalZ=1 AngleXU=0 Radius=4.5 StartAngle=4.71239 EndAngle=5.93412
    g7: LineSegment StartX=103.485 StartY=93.4609 StartZ=0 EndX=70.7276 EndY=3.46091 EndZ=0
FEATURE [Sketcher::SketchObject] Unfold_Sketch_Internal005
  ArcFitTolerance = 1e-06
  FullyConstrained = false
  MakeInternals = false
  sketch-geometry (1):
    g0: Circle CenterX=0 CenterY=50 CenterZ=0 NormalX=0 NormalY=0 NormalZ=-1 AngleXU=0 Radius=15
FEATURE [App::DocumentObjectGroup] Group007  label="sink_cutout_Group"
  Group = -> [Unfold005,Unfold_Sketch005,Unfold_Sketch_Outline005,Unfold_Sketch_Internal005]
FEATURE [TechDraw::DrawViewDimension] Dimension
  AngleOverride = false
  Arbitrary = false
  ArbitraryTolerances = false
  BoxCorners = (2) [(-97.5,-40.5,-1e-07),(97.5,40.5,1e-07)]
  EqualTolerance = true
  ExtensionAngle = 0
  FormatSpec = %.2w
  FormatSpecOverTolerance = %+.2w
  FormatSpecUnderTolerance = %+.2w
  Inverted = false
  LineAngle = 0
  LockPosition = false
  MeasureType = 1
  OverTolerance = 0
  References2D = -> [View]
  Rotation = 0
  ScaleType = 0
  TheoreticalExact = false
  Type = 1
  UnderTolerance = 0
  X = 0
  Y = 53.5692
FEATURE [TechDraw::DrawViewDimension] Dimension017
  AngleOverride = false
  Arbitrary = false
  ArbitraryTolerances = false
  BoxCorners = (2) [(-97.5,-40.5,-1e-07),(97.5,40.5,1e-07)]
  EqualTolerance = true
  ExtensionAngle = 0
  FormatSpec = %.2w
  FormatSpecOverTolerance = %+.2w
  FormatSpecUnderTolerance = %+.2w
  Inverted = false
  LineAngle = 0
  LockPosition = false
  MeasureType = 1
  OverTolerance = 0
  References2D = -> [View]
  Rotation = 0
  ScaleType = 0
  TheoreticalExact = false
  Type = 1
  UnderTolerance = 0
  X = 75
  Y = -62.9026
FEATURE [TechDraw::DrawViewDimension] Dimension018
  AngleOverride = false
  Arbitrary = false
  ArbitraryTolerances = false
  BoxCorners = (2) [(-97.5,-40.5,-1e-07),(97.5,40.5,1e-07)]
  EqualTolerance = true
  ExtensionAngle = 0
  FormatSpec = %.2w
  FormatSpecOverTolerance = %+.2w
  FormatSpecUnderTolerance = %+.2w
  Inverted = false
  LineAngle = 0
  LockPosition = false
  MeasureType = 1
  OverTolerance = 0
  References2D = -> [View]
  Rotation = 0
  ScaleType = 0
  TheoreticalExact = false
  Type = 2
  UnderTolerance = 0
  X = -115.728
  Y = 0
FEATURE [TechDraw::DrawPage] Page
  KeepUpdated = true
  NextBalloonIndex = 1
  ProjectionType = 0
  Template = -> Template
  Views = -> [View,View001,Dimension003,Dimension004,Dimension,Dimension017,Dimension018]
FEATURE [App::DocumentObjectGroup] Group002  label="bar_Group"
  Group = -> [Unfold,Unfold_Sketch,Unfold_Sketch_Outline,Unfold_Sketch_Internal,Unfold_Sketch_bends,Page]
FEATURE [Part::Feature] Unfold006
  shape: bbox 968.1 x 0.5 x 350.4 mm, 109 faces (baked)
FEATURE [Sketcher::SketchObject] Unfold_Sketch_Outline006
  ArcFitTolerance = 1e-06
  FullyConstrained = false
  MakeInternals = false
  sketch-geometry (42):
    g0: LineSegment StartX=-245.447 StartY=-442.677 StartZ=0 EndX=-237.361 EndY=-442.677 EndZ=0
    g1: LineSegment StartX=-236.952 StartY=-442.677 StartZ=0 EndX=-237.361 EndY=-442.677 EndZ=0
    g2: LineSegment StartX=-234.077 StartY=-445.114 StartZ=0 EndX=-236.952 EndY=-442.677 EndZ=0
    g3: LineSegment StartX=-234.077 StartY=-445.114 StartZ=0 EndX=-234.129 EndY=-445.176 EndZ=0
    g4: ArcOfCircle CenterX=-231.841 CenterY=-447.116 CenterZ=0 NormalX=0 NormalY=0 NormalZ=1 AngleXU=-2.39375 Radius=3 StartAngle=4.83213 EndAngle=6.28319
    g5: LineSegment StartX=-234.041 StartY=-449.156 StartZ=0 EndX=-203.176 EndY=-482.431 EndZ=0
    g6: ArcOfCircle CenterX=-199.51 CenterY=-479.031 CenterZ=0 NormalX=0 NormalY=0 NormalZ=1 AngleXU=-2.39375 Radius=5 StartAngle=-1.8e-15 EndAngle=1.5708
    g7: LineSegment StartX=-196.11 StartY=-482.696 StartZ=0 EndX=64.6114 EndY=-240.859 EndZ=0
    g8: ArcOfCircle CenterX=61.2111 CenterY=-237.194 CenterZ=0 NormalX=0 NormalY=0 NormalZ=1 AngleXU=-2.39375 Radius=5 StartAngle=1.5708 EndAngle=3.14159
    g9: LineSegment StartX=64.8769 StartY=-233.793 StartZ=0 EndX=9.39085 EndY=-173.975 EndZ=0
    g10: ArcOfCircle CenterX=6.45821 CenterY=-176.695 CenterZ=0 NormalX=0 NormalY=0 NormalZ=1 AngleXU=-2.39375 Radius=4 StartAngle=3.14159 EndAngle=4.37946
    g11: ArcOfCircle CenterX=2.02406 CenterY=-166.628 CenterZ=0 NormalX=0 NormalY=0 NormalZ=1 AngleXU=-2.39375 Radius=7 StartAngle=0.11974 EndAngle=1.23786
    g12: LineSegment StartX=-5.37755 StartY=-169.53 StartZ=0 EndX=-2.50267 EndY=-171.968 EndZ=0
    g13: ArcOfCircle CenterX=-0.850822 CenterY=-164.191 CenterZ=0 NormalX=0 NormalY=0 NormalZ=1 AngleXU=-1.5708 Radius=7 StartAngle=3.14159 EndAngle=5.57997
    g14: LineSegment StartX=3.01366 StartY=-157.191 StartZ=0 EndX=-0.850822 EndY=-157.191 EndZ=0
    g15: ArcOfCircle CenterX=3.01366 CenterY=-164.191 CenterZ=0 NormalX=0 NormalY=0 NormalZ=1 AngleXU=-1.5708 Radius=7 StartAngle=1.90373 EndAngle=3.14159
    g16: ArcOfCircle CenterX=13.4096 CenterY=-160.596 CenterZ=0 NormalX=0 NormalY=0 NormalZ=1 AngleXU=-1.5708 Radius=4 StartAngle=5.04532 EndAngle=6.28319
    g17: LineSegment StartX=95 StartY=-164.596 StartZ=0 EndX=13.4096 EndY=-164.596 EndZ=0
    g18: ArcOfCircle CenterX=95 CenterY=-159.596 CenterZ=0 NormalX=0 NormalY=0 NormalZ=1 AngleXU=-1.5708 Radius=5 StartAngle=0 EndAngle=1.5708
    g19: LineSegment StartX=100 StartY=159.596 StartZ=0 EndX=100 EndY=-159.596 EndZ=0
    g20: ArcOfCircle CenterX=95 CenterY=159.596 CenterZ=0 NormalX=0 NormalY=0 NormalZ=1 AngleXU=1.5708 Radius=5 StartAngle=4.71239 EndAngle=6.28319
    g21: LineSegment StartX=13.4096 StartY=164.596 StartZ=0 EndX=95 EndY=164.596 EndZ=0
    g22: ArcOfCircle CenterX=13.4096 CenterY=160.596 CenterZ=0 NormalX=0 NormalY=0 NormalZ=1 AngleXU=1.5708 Radius=4 StartAngle=9e-16 EndAngle=1.23786
    g23: ArcOfCircle CenterX=3.01366 CenterY=164.191 CenterZ=0 NormalX=0 NormalY=0 NormalZ=1 AngleXU=1.5708 Radius=7 StartAngle=3.14159 EndAngle=4.37946
    g24: LineSegment StartX=3.01366 StartY=157.191 StartZ=0 EndX=-0.850822 EndY=157.191 EndZ=0
    g25: ArcOfCircle CenterX=-0.850822 CenterY=164.191 CenterZ=0 NormalX=0 NormalY=0 NormalZ=1 AngleXU=1.5708 Radius=7 StartAngle=0.703217 EndAngle=3.14159
    g26: LineSegment StartX=-2.50267 StartY=171.968 StartZ=0 EndX=-5.37755 EndY=169.53 EndZ=0
    g27: ArcOfCircle CenterX=2.02406 CenterY=166.628 CenterZ=0 NormalX=0 NormalY=0 NormalZ=1 AngleXU=2.39375 Radius=7 StartAngle=5.04532 EndAngle=6.16345
    g28: ArcOfCircle CenterX=6.45821 CenterY=176.695 CenterZ=0 NormalX=0 NormalY=0 NormalZ=1 AngleXU=2.39375 Radius=4 StartAngle=1.90373 EndAngle=3.14159
    g29: LineSegment StartX=64.8769 StartY=233.793 StartZ=0 EndX=9.39085 EndY=173.975 EndZ=0
    g30: ArcOfCircle CenterX=61.2111 CenterY=237.194 CenterZ=0 NormalX=0 NormalY=0 NormalZ=1 AngleXU=2.39375 Radius=5 StartAngle=3.14159 EndAngle=4.71239
    g31: LineSegment StartX=-196.11 StartY=482.696 StartZ=0 EndX=64.6114 EndY=240.859 EndZ=0
    g32: ArcOfCircle CenterX=-199.51 CenterY=479.031 CenterZ=0 NormalX=0 NormalY=0 NormalZ=1 AngleXU=2.39375 Radius=5 StartAngle=4.71239 EndAngle=6.28319
    g33: LineSegment StartX=-234.041 StartY=449.156 StartZ=0 EndX=-203.176 EndY=482.431 EndZ=0
    g34: ArcOfCircle CenterX=-231.841 CenterY=447.116 CenterZ=0 NormalX=0 NormalY=0 NormalZ=1 AngleXU=2.39375 Radius=3 StartAngle=-9e-16 EndAngle=1.45106
    g35: LineSegment StartX=-234.077 StartY=445.114 StartZ=0 EndX=-234.129 EndY=445.176 EndZ=0
    g36: LineSegment StartX=-236.952 StartY=442.677 StartZ=0 EndX=-234.077 EndY=445.114 EndZ=0
    g37: LineSegment StartX=-237.361 StartY=442.677 StartZ=0 EndX=-236.952 EndY=442.677 EndZ=0
    g38: LineSegment StartX=-237.361 StartY=442.677 StartZ=0 EndX=-245.447 EndY=442.677 EndZ=0
    g39: ArcOfCircle CenterX=-245.447 CenterY=437.677 CenterZ=0 NormalX=0 NormalY=0 NormalZ=1 AngleXU=1.5708 Radius=5 StartAngle=0 EndAngle=1.5708
    g40: LineSegment StartX=-250.447 StartY=-437.677 StartZ=0 EndX=-250.447 EndY=437.677 EndZ=0
    g41: ArcOfCircle CenterX=-245.447 CenterY=-437.677 CenterZ=0 NormalX=0 NormalY=0 NormalZ=1 AngleXU=-1.5708 Radius=5 StartAngle=4.71239 EndAngle=6.28319
FEATURE [Sketcher::SketchObject] Unfold_Sketch_Internal006
  ArcFitTolerance = 1e-06
  FullyConstrained = false
  MakeInternals = false
  sketch-geometry (67):
    g0: LineSegment StartX=-91.1271 StartY=-71.1974 StartZ=0 EndX=-181.127 EndY=-103.955 EndZ=0
    g1: ArcOfCircle CenterX=-182.837 CenterY=-99.2563 CenterZ=0 NormalX=0 NormalY=0 NormalZ=1 AngleXU=-1.5708 Radius=5 StartAngle=4.71239 EndAngle=6.63225
    g2: LineSegment StartX=-187.837 StartY=-99.2563 StartZ=0 EndX=-187.837 EndY=99.2563 EndZ=0
    g3: ArcOfCircle CenterX=-182.837 CenterY=99.2563 CenterZ=0 NormalX=0 NormalY=0 NormalZ=1 AngleXU=1.5708 Radius=5 StartAngle=5.93412 EndAngle=7.85398
    g4: LineSegment StartX=-181.127 StartY=103.955 StartZ=0 EndX=-91.1271 EndY=71.1974 EndZ=0
    g5: ArcOfCircle CenterX=-92.8372 CenterY=66.499 CenterZ=0 NormalX=0 NormalY=0 NormalZ=1 AngleXU=1.5708 Radius=5 StartAngle=4.71239 EndAngle=5.93412
    g6: LineSegment StartX=-87.8372 StartY=66.499 StartZ=0 EndX=-87.8372 EndY=-66.499 EndZ=0
    g7: ArcOfCircle CenterX=-92.8372 CenterY=-66.499 CenterZ=0 NormalX=0 NormalY=0 NormalZ=1 AngleXU=-1.5708 Radius=5 StartAngle=0.349066 EndAngle=1.5708
    g8: ArcOfCircle CenterX=-0.850822 CenterY=-103 CenterZ=0 NormalX=0 NormalY=0 NormalZ=1 AngleXU=1.5708 Radius=3 StartAngle=0 EndAngle=1.5708
    g9: LineSegment StartX=-3.85082 StartY=-103 StartZ=0 EndX=-3.85082 EndY=-147 EndZ=0
    g10: ArcOfCircle CenterX=-0.850822 CenterY=-147 CenterZ=0 NormalX=0 NormalY=0 NormalZ=1 AngleXU=1.5708 Radius=3 StartAngle=1.5708 EndAngle=3.14159
    g11: LineSegment StartX=-0.850822 StartY=-150 StartZ=0 EndX=3.01366 EndY=-150 EndZ=0
    g12: ArcOfCircle CenterX=3.01366 CenterY=-148 CenterZ=0 NormalX=0 NormalY=0 NormalZ=1 AngleXU=1.5708 Radius=2 StartAngle=3.14159 EndAngle=4.71239
    g13: LineSegment StartX=5.01366 StartY=-102 StartZ=0 EndX=5.01366 EndY=-148 EndZ=0
    g14: ArcOfCircle CenterX=3.01366 CenterY=-102 CenterZ=0 NormalX=0 NormalY=0 NormalZ=1 AngleXU=1.5708 Radius=2 StartAngle=4.71239 EndAngle=6.28319
    g15: LineSegment StartX=-0.850822 StartY=-100 StartZ=0 EndX=3.01366 EndY=-100 EndZ=0
    g16: ArcOfCircle CenterX=-0.850822 CenterY=147 CenterZ=0 NormalX=0 NormalY=0 NormalZ=1 AngleXU=1.5708 Radius=3 StartAngle=0 EndAngle=1.5708
    g17: LineSegment StartX=-3.85082 StartY=147 StartZ=0 EndX=-3.85082 EndY=103 EndZ=0
    g18: ArcOfCircle CenterX=-0.850822 CenterY=103 CenterZ=0 NormalX=0 NormalY=0 NormalZ=1 AngleXU=1.5708 Radius=3 StartAngle=1.5708 EndAngle=3.14159
    g19: LineSegment StartX=3.01366 StartY=100 StartZ=0 EndX=-0.850822 EndY=100 EndZ=0
    g20: ArcOfCircle CenterX=3.01366 CenterY=102 CenterZ=0 NormalX=0 NormalY=0 NormalZ=1 AngleXU=1.5708 Radius=2 StartAngle=3.14159 EndAngle=4.71239
    g21: LineSegment StartX=5.01366 StartY=148 StartZ=0 EndX=5.01366 EndY=102 EndZ=0
    g22: ArcOfCircle CenterX=3.01366 CenterY=148 CenterZ=0 NormalX=0 NormalY=0 NormalZ=1 AngleXU=1.5708 Radius=2 StartAngle=4.71239 EndAngle=6.28319
    g23: LineSegment StartX=-0.850822 StartY=150 StartZ=0 EndX=3.01366 EndY=150 EndZ=0
    g24: ArcOfCircle CenterX=-0.850822 CenterY=84.5 CenterZ=0 NormalX=0 NormalY=0 NormalZ=1 AngleXU=1.5708 Radius=3 StartAngle=0 EndAngle=1.5708
    g25: LineSegment StartX=-3.85082 StartY=84.5 StartZ=0 EndX=-3.85082 EndY=40.5 EndZ=0
    g26: ArcOfCircle CenterX=-0.850822 CenterY=40.5 CenterZ=0 NormalX=0 NormalY=0 NormalZ=1 AngleXU=1.5708 Radius=3 StartAngle=1.5708 EndAngle=3.14159
    g27: LineSegment StartX=3.01366 StartY=37.5 StartZ=0 EndX=-0.850822 EndY=37.5 EndZ=0
    g28: ArcOfCircle CenterX=3.01366 CenterY=39.5 CenterZ=0 NormalX=0 NormalY=0 NormalZ=1 AngleXU=1.5708 Radius=2 StartAngle=3.14159 EndAngle=4.71239
    g29: LineSegment StartX=5.01366 StartY=85.5 StartZ=0 EndX=5.01366 EndY=39.5 EndZ=0
    g30: ArcOfCircle CenterX=3.01366 CenterY=85.5 CenterZ=0 NormalX=0 NormalY=0 NormalZ=1 AngleXU=1.5708 Radius=2 StartAngle=4.71239 EndAngle=6.28319
    g31: LineSegment StartX=-0.850822 StartY=87.5 StartZ=0 EndX=3.01366 EndY=87.5 EndZ=0
    g32: ArcOfCircle CenterX=-0.850822 CenterY=22 CenterZ=0 NormalX=0 NormalY=0 NormalZ=1 AngleXU=1.5708 Radius=3 StartAngle=0 EndAngle=1.5708
    g33: LineSegment StartX=-3.85082 StartY=22 StartZ=0 EndX=-3.85082 EndY=-22 EndZ=0
    g34: ArcOfCircle CenterX=-0.850822 CenterY=-22 CenterZ=0 NormalX=0 NormalY=0 NormalZ=1 AngleXU=1.5708 Radius=3 StartAngle=1.5708 EndAngle=3.14159
    g35: LineSegment StartX=3.01366 StartY=-25 StartZ=0 EndX=-0.850822 EndY=-25 EndZ=0
    g36: ArcOfCircle CenterX=3.01366 CenterY=-23 CenterZ=0 NormalX=0 NormalY=0 NormalZ=1 AngleXU=1.5708 Radius=2 StartAngle=3.14159 EndAngle=4.71239
    g37: LineSegment StartX=5.01366 StartY=23 StartZ=0 EndX=5.01366 EndY=-23 EndZ=0
    g38: ArcOfCircle CenterX=3.01366 CenterY=23 CenterZ=0 NormalX=0 NormalY=0 NormalZ=1 AngleXU=1.5708 Radius=2 StartAngle=4.71239 EndAngle=6.28319
    g39: LineSegment StartX=-0.850822 StartY=25 StartZ=0 EndX=3.01366 EndY=25 EndZ=0
    g40: ArcOfCircle CenterX=-0.850822 CenterY=-40.5 CenterZ=0 NormalX=0 NormalY=0 NormalZ=1 AngleXU=1.5708 Radius=3 StartAngle=0 EndAngle=1.5708
    g41: LineSegment StartX=-3.85082 StartY=-40.5 StartZ=0 EndX=-3.85082 EndY=-84.5 EndZ=0
    g42: ArcOfCircle CenterX=-0.850822 CenterY=-84.5 CenterZ=0 NormalX=0 NormalY=0 NormalZ=1 AngleXU=1.5708 Radius=3 StartAngle=1.5708 EndAngle=3.14159
    g43: LineSegment StartX=3.01366 StartY=-87.5 StartZ=0 EndX=-0.850822 EndY=-87.5 EndZ=0
    g44: ArcOfCircle CenterX=3.01366 CenterY=-85.5 CenterZ=0 NormalX=0 NormalY=0 NormalZ=1 AngleXU=1.5708 Radius=2 StartAngle=3.14159 EndAngle=4.71239
    g45: LineSegment StartX=5.01366 StartY=-39.5 StartZ=0 EndX=5.01366 EndY=-85.5 EndZ=0
    g46: ArcOfCircle CenterX=3.01366 CenterY=-39.5 CenterZ=0 NormalX=0 NormalY=0 NormalZ=1 AngleXU=1.5708 Radius=2 StartAngle=4.71239 EndAngle=6.28319
    g47: LineSegment StartX=-0.850822 StartY=-37.5 StartZ=0 EndX=3.01366 EndY=-37.5 EndZ=0
    g48: Circle CenterX=-67.9966 CenterY=355.679 CenterZ=0 NormalX=0 NormalY=0 NormalZ=1 AngleXU=2.39375 Radius=1.7
    g49: Circle CenterX=60.5311 CenterY=-236.461 CenterZ=0 NormalX=0 NormalY=0 NormalZ=1 AngleXU=-2.39375 Radius=1.7
    g50: Circle CenterX=-67.9966 CenterY=-355.679 CenterZ=0 NormalX=0 NormalY=0 NormalZ=1 AngleXU=-2.39375 Radius=1.7
    g51: Circle CenterX=60.5311 CenterY=236.461 CenterZ=0 NormalX=0 NormalY=0 NormalZ=1 AngleXU=2.39375 Radius=1.7
    g52: Circle CenterX=-227.127 CenterY=-441.905 CenterZ=0 NormalX=0 NormalY=0 NormalZ=1 AngleXU=-2.39375 Radius=1.7
    g53: Circle CenterX=-196.524 CenterY=-474.897 CenterZ=0 NormalX=0 NormalY=0 NormalZ=1 AngleXU=-2.39375 Radius=1.7
    g54: Circle CenterX=-196.524 CenterY=474.897 CenterZ=0 NormalX=0 NormalY=0 NormalZ=1 AngleXU=2.39375 Radius=1.7
    g55: Circle CenterX=-227.127 CenterY=441.905 CenterZ=0 NormalX=0 NormalY=0 NormalZ=1 AngleXU=2.39375 Radius=1.7
    g56: Circle CenterX=-77.8372 CenterY=-70 CenterZ=0 NormalX=0 NormalY=0 NormalZ=1 AngleXU=1.5708 Radius=1.7
    g57: Circle CenterX=-77.8372 CenterY=70 CenterZ=0 NormalX=0 NormalY=0 NormalZ=1 AngleXU=1.5708 Radius=1.7
    g58: Circle CenterX=-77.8372 CenterY=1.42e-14 CenterZ=0 NormalX=0 NormalY=0 NormalZ=1 AngleXU=1.5708 Radius=1.7
    g59: Circle CenterX=94 CenterY=0 CenterZ=0 NormalX=0 NormalY=0 NormalZ=1 AngleXU=1.5708 Radius=1.7
    g60: Circle CenterX=-197.837 CenterY=70 CenterZ=0 NormalX=0 NormalY=0 NormalZ=1 AngleXU=-1.5708 Radius=1.7
    g61: Circle CenterX=-197.837 CenterY=-70 CenterZ=0 NormalX=0 NormalY=0 NormalZ=1 AngleXU=-1.5708 Radius=1.7
    g62: Circle CenterX=34 CenterY=-159.596 CenterZ=0 NormalX=0 NormalY=0 NormalZ=1 AngleXU=1.5708 Radius=1.7
    g63: Circle CenterX=94 CenterY=-159.596 CenterZ=0 NormalX=0 NormalY=0 NormalZ=1 AngleXU=1.5708 Radius=1.7
    g64: Circle CenterX=34 CenterY=159.596 CenterZ=0 NormalX=0 NormalY=0 NormalZ=1 AngleXU=1.5708 Radius=1.7
    g65: Circle CenterX=94 CenterY=159.596 CenterZ=0 NormalX=0 NormalY=0 NormalZ=1 AngleXU=1.5708 Radius=1.7
    g66: Circle CenterX=-197.837 CenterY=0 CenterZ=0 NormalX=0 NormalY=0 NormalZ=1 AngleXU=-1.5708 Radius=1.7
FEATURE [Sketcher::SketchObject] Unfold_Sketch_bends004
  ArcFitTolerance = 1e-06
  FullyConstrained = false
  MakeInternals = false
  sketch-geometry (10):
    g0: LineSegment StartX=-241.219 StartY=442.677 StartZ=0 EndX=-241.219 EndY=-442.677 EndZ=0
    g1: LineSegment StartX=-237.156 StartY=442.677 StartZ=0 EndX=-237.156 EndY=-442.677 EndZ=0
    g2: LineSegment StartX=-235.515 StartY=443.896 StartZ=0 EndX=-3.94011 EndY=170.749 EndZ=0
    g3: LineSegment StartX=1.08142 StartY=157.191 StartZ=0 EndX=1.08142 EndY=150 EndZ=0
    g4: LineSegment StartX=1.08142 StartY=100 StartZ=0 EndX=1.08142 EndY=87.5 EndZ=0
    g5: LineSegment StartX=1.08142 StartY=37.5 StartZ=0 EndX=1.08142 EndY=25 EndZ=0
    g6: LineSegment StartX=1.08142 StartY=-25 StartZ=0 EndX=1.08142 EndY=-37.5 EndZ=0
    g7: LineSegment StartX=1.08142 StartY=-87.5 StartZ=0 EndX=1.08142 EndY=-100 EndZ=0
    g8: LineSegment StartX=-235.515 StartY=-443.896 StartZ=0 EndX=-3.94011 EndY=-170.749 EndZ=0
    g9: LineSegment StartX=1.08142 StartY=-150 StartZ=0 EndX=1.08142 EndY=-157.191 EndZ=0
FEATURE [Sketcher::SketchObject] Unfold_Sketch006
  ArcFitTolerance = 1e-06
  ExternalGeometry = -> [Unfold_Sketch_bends004]
  FullyConstrained = false
  MakeInternals = false
  sketch-geometry (115):
    g0: LineSegment StartX=-245.447 StartY=-442.677 StartZ=0 EndX=-237.361 EndY=-442.677 EndZ=0
    g1: LineSegment StartX=-236.952 StartY=-442.677 StartZ=0 EndX=-237.361 EndY=-442.677 EndZ=0
    g2: LineSegment StartX=-234.077 StartY=-445.114 StartZ=0 EndX=-236.952 EndY=-442.677 EndZ=0
    g3: LineSegment StartX=-234.077 StartY=-445.114 StartZ=0 EndX=-234.129 EndY=-445.176 EndZ=0
    g4: ArcOfCircle CenterX=-231.841 CenterY=-447.116 CenterZ=0 NormalX=0 NormalY=0 NormalZ=1 AngleXU=-2.39375 Radius=3 StartAngle=4.83213 EndAngle=6.28319
    g5: LineSegment StartX=-234.041 StartY=-449.156 StartZ=0 EndX=-203.176 EndY=-482.431 EndZ=0
    g6: ArcOfCircle CenterX=-199.51 CenterY=-479.031 CenterZ=0 NormalX=0 NormalY=0 NormalZ=1 AngleXU=-2.39375 Radius=5 StartAngle=-1.8e-15 EndAngle=1.5708
    g7: LineSegment StartX=-196.11 StartY=-482.696 StartZ=0 EndX=64.6114 EndY=-240.859 EndZ=0
    g8: ArcOfCircle CenterX=61.2111 CenterY=-237.194 CenterZ=0 NormalX=0 NormalY=0 NormalZ=1 AngleXU=-2.39375 Radius=5 StartAngle=1.5708 EndAngle=3.14159
    g9: LineSegment StartX=64.8769 StartY=-233.793 StartZ=0 EndX=9.39085 EndY=-173.975 EndZ=0
    g10: ArcOfCircle CenterX=6.45821 CenterY=-176.695 CenterZ=0 NormalX=0 NormalY=0 NormalZ=1 AngleXU=-2.39375 Radius=4 StartAngle=3.14159 EndAngle=4.37946
    g11: ArcOfCircle CenterX=2.02406 CenterY=-166.628 CenterZ=0 NormalX=0 NormalY=0 NormalZ=1 AngleXU=-2.39375 Radius=7 StartAngle=0.11974 EndAngle=1.23786
    g12: LineSegment StartX=-5.37755 StartY=-169.53 StartZ=0 EndX=-2.50267 EndY=-171.968 EndZ=0
    g13: ArcOfCircle CenterX=-0.850822 CenterY=-164.191 CenterZ=0 NormalX=0 NormalY=0 NormalZ=1 AngleXU=-1.5708 Radius=7 StartAngle=3.14159 EndAngle=5.57997
    g14: LineSegment StartX=3.01366 StartY=-157.191 StartZ=0 EndX=-0.850822 EndY=-157.191 EndZ=0
    g15: ArcOfCircle CenterX=3.01366 CenterY=-164.191 CenterZ=0 NormalX=0 NormalY=0 NormalZ=1 AngleXU=-1.5708 Radius=7 StartAngle=1.90373 EndAngle=3.14159
    g16: ArcOfCircle CenterX=13.4096 CenterY=-160.596 CenterZ=0 NormalX=0 NormalY=0 NormalZ=1 AngleXU=-1.5708 Radius=4 StartAngle=5.04532 EndAngle=6.28319
    g17: LineSegment StartX=95 StartY=-164.596 StartZ=0 EndX=13.4096 EndY=-164.596 EndZ=0
    g18: ArcOfCircle CenterX=95 CenterY=-159.596 CenterZ=0 NormalX=0 NormalY=0 NormalZ=1 AngleXU=-1.5708 Radius=5 StartAngle=0 EndAngle=1.5708
    g19: LineSegment StartX=100 StartY=159.596 StartZ=0 EndX=100 EndY=-159.596 EndZ=0
    g20: ArcOfCircle CenterX=95 CenterY=159.596 CenterZ=0 NormalX=0 NormalY=0 NormalZ=1 AngleXU=1.5708 Radius=5 StartAngle=4.71239 EndAngle=6.28319
    g21: LineSegment StartX=13.4096 StartY=164.596 StartZ=0 EndX=95 EndY=164.596 EndZ=0
    g22: ArcOfCircle CenterX=13.4096 CenterY=160.596 CenterZ=0 NormalX=0 NormalY=0 NormalZ=1 AngleXU=1.5708 Radius=4 StartAngle=9e-16 EndAngle=1.23786
    g23: ArcOfCircle CenterX=3.01366 CenterY=164.191 CenterZ=0 NormalX=0 NormalY=0 NormalZ=1 AngleXU=1.5708 Radius=7 StartAngle=3.14159 EndAngle=4.37946
    g24: LineSegment StartX=3.01366 StartY=157.191 StartZ=0 EndX=-0.850822 EndY=157.191 EndZ=0
    g25: ArcOfCircle CenterX=-0.850822 CenterY=164.191 CenterZ=0 NormalX=0 NormalY=0 NormalZ=1 AngleXU=1.5708 Radius=7 StartAngle=0.703217 EndAngle=3.14159
    g26: LineSegment StartX=-2.50267 StartY=171.968 StartZ=0 EndX=-5.37755 EndY=169.53 EndZ=0
    g27: ArcOfCircle CenterX=2.02406 CenterY=166.628 CenterZ=0 NormalX=0 NormalY=0 NormalZ=1 AngleXU=2.39375 Radius=7 StartAngle=5.04532 EndAngle=6.16345
    g28: ArcOfCircle CenterX=6.45821 CenterY=176.695 CenterZ=0 NormalX=0 NormalY=0 NormalZ=1 AngleXU=2.39375 Radius=4 StartAngle=1.90373 EndAngle=3.14159
    g29: LineSegment StartX=64.8769 StartY=233.793 StartZ=0 EndX=9.39085 EndY=173.975 EndZ=0
    g30: ArcOfCircle CenterX=61.2111 CenterY=237.194 CenterZ=0 NormalX=0 NormalY=0 NormalZ=1 AngleXU=2.39375 Radius=5 StartAngle=3.14159 EndAngle=4.71239
    g31: LineSegment StartX=-196.11 StartY=482.696 StartZ=0 EndX=64.6114 EndY=240.859 EndZ=0
    g32: ArcOfCircle CenterX=-199.51 CenterY=479.031 CenterZ=0 NormalX=0 NormalY=0 NormalZ=1 AngleXU=2.39375 Radius=5 StartAngle=4.71239 EndAngle=6.28319
    g33: LineSegment StartX=-234.041 StartY=449.156 StartZ=0 EndX=-203.176 EndY=482.431 EndZ=0
    g34: ArcOfCircle CenterX=-231.841 CenterY=447.116 CenterZ=0 NormalX=0 NormalY=0 NormalZ=1 AngleXU=2.39375 Radius=3 StartAngle=-9e-16 EndAngle=1.45106
    g35: LineSegment StartX=-234.077 StartY=445.114 StartZ=0 EndX=-234.129 EndY=445.176 EndZ=0
    g36: LineSegment StartX=-236.952 StartY=442.677 StartZ=0 EndX=-234.077 EndY=445.114 EndZ=0
    g37: LineSegment StartX=-237.361 StartY=442.677 StartZ=0 EndX=-236.952 EndY=442.677 EndZ=0
    g38: LineSegment StartX=-237.361 StartY=442.677 StartZ=0 EndX=-245.447 EndY=442.677 EndZ=0
    g39: ArcOfCircle CenterX=-245.447 CenterY=437.677 CenterZ=0 NormalX=0 NormalY=0 NormalZ=1 AngleXU=1.5708 Radius=5 StartAngle=0 EndAngle=1.5708
    g40: LineSegment StartX=-250.447 StartY=-437.677 StartZ=0 EndX=-250.447 EndY=437.677 EndZ=0
    g41: ArcOfCircle CenterX=-245.447 CenterY=-437.677 CenterZ=0 NormalX=0 NormalY=0 NormalZ=1 AngleXU=-1.5708 Radius=5 StartAngle=4.71239 EndAngle=6.28319
    g42: LineSegment StartX=-91.1271 StartY=-71.1974 StartZ=0 EndX=-181.127 EndY=-103.955 EndZ=0
    g43: ArcOfCircle CenterX=-182.837 CenterY=-99.2563 CenterZ=0 NormalX=0 NormalY=0 NormalZ=1 AngleXU=-1.5708 Radius=5 StartAngle=4.71239 EndAngle=6.63225
    g44: LineSegment StartX=-187.837 StartY=-99.2563 StartZ=0 EndX=-187.837 EndY=99.2563 EndZ=0
    g45: ArcOfCircle CenterX=-182.837 CenterY=99.2563 CenterZ=0 NormalX=0 NormalY=0 NormalZ=1 AngleXU=1.5708 Radius=5 StartAngle=5.93412 EndAngle=7.85398
    g46: LineSegment StartX=-181.127 StartY=103.955 StartZ=0 EndX=-91.1271 EndY=71.1974 EndZ=0
    g47: ArcOfCircle CenterX=-92.8372 CenterY=66.499 CenterZ=0 NormalX=0 NormalY=0 NormalZ=1 AngleXU=1.5708 Radius=5 StartAngle=4.71239 EndAngle=5.93412
    g48: LineSegment StartX=-87.8372 StartY=66.499 StartZ=0 EndX=-87.8372 EndY=-66.499 EndZ=0
    g49: ArcOfCircle CenterX=-92.8372 CenterY=-66.499 CenterZ=0 NormalX=0 NormalY=0 NormalZ=1 AngleXU=-1.5708 Radius=5 StartAngle=0.349066 EndAngle=1.5708
    g50: ArcOfCircle CenterX=-0.850822 CenterY=-103 CenterZ=0 NormalX=0 NormalY=0 NormalZ=1 AngleXU=1.5708 Radius=3 StartAngle=0 EndAngle=1.5708
    g51: LineSegment StartX=-0.850822 StartY=-100 StartZ=0 EndX=3.01366 EndY=-100 EndZ=0
    g52: ArcOfCircle CenterX=3.01366 CenterY=-102 CenterZ=0 NormalX=0 NormalY=0 NormalZ=1 AngleXU=1.5708 Radius=2 StartAngle=4.71239 EndAngle=6.28319
    g53: LineSegment StartX=5.01366 StartY=-102 StartZ=0 EndX=5.01366 EndY=-148 EndZ=0
    g54: ArcOfCircle CenterX=3.01366 CenterY=-148 CenterZ=0 NormalX=0 NormalY=0 NormalZ=1 AngleXU=1.5708 Radius=2 StartAngle=3.14159 EndAngle=4.71239
    g55: LineSegment StartX=-0.850822 StartY=-150 StartZ=0 EndX=3.01366 EndY=-150 EndZ=0
    g56: ArcOfCircle CenterX=-0.850822 CenterY=-147 CenterZ=0 NormalX=0 NormalY=0 NormalZ=1 AngleXU=1.5708 Radius=3 StartAngle=1.5708 EndAngle=3.14159
    g57: LineSegment StartX=-3.85082 StartY=-103 StartZ=0 EndX=-3.85082 EndY=-147 EndZ=0
    g58: ArcOfCircle CenterX=-0.850822 CenterY=-40.5 CenterZ=0 NormalX=0 NormalY=0 NormalZ=1 AngleXU=1.5708 Radius=3 StartAngle=0 EndAngle=1.5708
    g59: LineSegment StartX=-0.850822 StartY=-37.5 StartZ=0 EndX=3.01366 EndY=-37.5 EndZ=0
    g60: ArcOfCircle CenterX=3.01366 CenterY=-39.5 CenterZ=0 NormalX=0 NormalY=0 NormalZ=1 AngleXU=1.5708 Radius=2 StartAngle=4.71239 EndAngle=6.28319
    g61: LineSegment StartX=5.01366 StartY=-39.5 StartZ=0 EndX=5.01366 EndY=-85.5 EndZ=0
    g62: ArcOfCircle CenterX=3.01366 CenterY=-85.5 CenterZ=0 NormalX=0 NormalY=0 NormalZ=1 AngleXU=1.5708 Radius=2 StartAngle=3.14159 EndAngle=4.71239
    g63: LineSegment StartX=3.01366 StartY=-87.5 StartZ=0 EndX=-0.850822 EndY=-87.5 EndZ=0
    g64: ArcOfCircle CenterX=-0.850822 CenterY=-84.5 CenterZ=0 NormalX=0 NormalY=0 NormalZ=1 AngleXU=1.5708 Radius=3 StartAngle=1.5708 EndAngle=3.14159
    g65: LineSegment StartX=-3.85082 StartY=-40.5 StartZ=0 EndX=-3.85082 EndY=-84.5 EndZ=0
    g66: ArcOfCircle CenterX=-0.850822 CenterY=84.5 CenterZ=0 NormalX=0 NormalY=0 NormalZ=1 AngleXU=1.5708 Radius=3 StartAngle=0 EndAngle=1.5708
    g67: LineSegment StartX=-0.850822 StartY=87.5 StartZ=0 EndX=3.01366 EndY=87.5 EndZ=0
    g68: ArcOfCircle CenterX=3.01366 CenterY=85.5 CenterZ=0 NormalX=0 NormalY=0 NormalZ=1 AngleXU=1.5708 Radius=2 StartAngle=4.71239 EndAngle=6.28319
    g69: LineSegment StartX=5.01366 StartY=85.5 StartZ=0 EndX=5.01366 EndY=39.5 EndZ=0
    g70: ArcOfCircle CenterX=3.01366 CenterY=39.5 CenterZ=0 NormalX=0 NormalY=0 NormalZ=1 AngleXU=1.5708 Radius=2 StartAngle=3.14159 EndAngle=4.71239
    g71: LineSegment StartX=3.01366 StartY=37.5 StartZ=0 EndX=-0.850822 EndY=37.5 EndZ=0
    g72: ArcOfCircle CenterX=-0.850822 CenterY=40.5 CenterZ=0 NormalX=0 NormalY=0 NormalZ=1 AngleXU=1.5708 Radius=3 StartAngle=1.5708 EndAngle=3.14159
    g73: LineSegment StartX=-3.85082 StartY=84.5 StartZ=0 EndX=-3.85082 EndY=40.5 EndZ=0
    g74: ArcOfCircle CenterX=-0.850822 CenterY=22 CenterZ=0 NormalX=0 NormalY=0 NormalZ=1 AngleXU=1.5708 Radius=3 StartAngle=0 EndAngle=1.5708
    g75: LineSegment StartX=-0.850822 StartY=25 StartZ=0 EndX=3.01366 EndY=25 EndZ=0
    g76: ArcOfCircle CenterX=3.01366 CenterY=23 CenterZ=0 NormalX=0 NormalY=0 NormalZ=1 AngleXU=1.5708 Radius=2 StartAngle=4.71239 EndAngle=6.28319
    g77: LineSegment StartX=5.01366 StartY=23 StartZ=0 EndX=5.01366 EndY=-23 EndZ=0
    g78: ArcOfCircle CenterX=3.01366 CenterY=-23 CenterZ=0 NormalX=0 NormalY=0 NormalZ=1 AngleXU=1.5708 Radius=2 StartAngle=3.14159 EndAngle=4.71239
    g79: LineSegment StartX=3.01366 StartY=-25 StartZ=0 EndX=-0.850822 EndY=-25 EndZ=0
    g80: ArcOfCircle CenterX=-0.850822 CenterY=-22 CenterZ=0 NormalX=0 NormalY=0 NormalZ=1 AngleXU=1.5708 Radius=3 StartAngle=1.5708 EndAngle=3.14159
    g81: LineSegment StartX=-3.85082 StartY=22 StartZ=0 EndX=-3.85082 EndY=-22 EndZ=0
    g82: ArcOfCircle CenterX=-0.850822 CenterY=147 CenterZ=0 NormalX=0 NormalY=0 NormalZ=1 AngleXU=1.5708 Radius=3 StartAngle=0 EndAngle=1.5708
    g83: LineSegment StartX=-0.850822 StartY=150 StartZ=0 EndX=3.01366 EndY=150 EndZ=0
    g84: ArcOfCircle CenterX=3.01366 CenterY=148 CenterZ=0 NormalX=0 NormalY=0 NormalZ=1 AngleXU=1.5708 Radius=2 StartAngle=4.71239 EndAngle=6.28319
    g85: LineSegment StartX=5.01366 StartY=148 StartZ=0 EndX=5.01366 EndY=102 EndZ=0
    g86: ArcOfCircle CenterX=3.01366 CenterY=102 CenterZ=0 NormalX=0 NormalY=0 NormalZ=1 AngleXU=1.5708 Radius=2 StartAngle=3.14159 EndAngle=4.71239
    g87: LineSegment StartX=3.01366 StartY=100 StartZ=0 EndX=-0.850822 EndY=100 EndZ=0
    g88: ArcOfCircle CenterX=-0.850822 CenterY=103 CenterZ=0 NormalX=0 NormalY=0 NormalZ=1 AngleXU=1.5708 Radius=3 StartAngle=1.5708 EndAngle=3.14159
    g89: LineSegment StartX=-3.85082 StartY=147 StartZ=0 EndX=-3.85082 EndY=103 EndZ=0
    g90: Circle CenterX=-77.8372 CenterY=70 CenterZ=0 NormalX=0 NormalY=0 NormalZ=1 AngleXU=1.5708 Radius=1.7
    g91: Circle CenterX=-77.8372 CenterY=-70 CenterZ=0 NormalX=0 NormalY=0 NormalZ=1 AngleXU=1.5708 Radius=1.7
    g92: Circle CenterX=-77.8372 CenterY=1.42e-14 CenterZ=0 NormalX=0 NormalY=0 NormalZ=1 AngleXU=1.5708 Radius=1.7
    g93: Circle CenterX=94 CenterY=0 CenterZ=0 NormalX=0 NormalY=0 NormalZ=1 AngleXU=1.5708 Radius=1.7
    g94: Circle CenterX=60.5311 CenterY=236.461 CenterZ=0 NormalX=0 NormalY=0 NormalZ=1 AngleXU=2.39375 Radius=1.7
    g95: Circle CenterX=-67.9966 CenterY=-355.679 CenterZ=0 NormalX=0 NormalY=0 NormalZ=1 AngleXU=-2.39375 Radius=1.7
    g96: Circle CenterX=94 CenterY=159.596 CenterZ=0 NormalX=0 NormalY=0 NormalZ=1 AngleXU=1.5708 Radius=1.7
    g97: Circle CenterX=60.5311 CenterY=-236.461 CenterZ=0 NormalX=0 NormalY=0 NormalZ=1 AngleXU=-2.39375 Radius=1.7
    g98: Circle CenterX=34 CenterY=159.596 CenterZ=0 NormalX=0 NormalY=0 NormalZ=1 AngleXU=1.5708 Radius=1.7
    g99: Circle CenterX=94 CenterY=-159.596 CenterZ=0 NormalX=0 NormalY=0 NormalZ=1 AngleXU=1.5708 Radius=1.7
    g100: Circle CenterX=34 CenterY=-159.596 CenterZ=0 NormalX=0 NormalY=0 NormalZ=1 AngleXU=1.5708 Radius=1.7
    g101: Circle CenterX=-67.9966 CenterY=355.679 CenterZ=0 NormalX=0 NormalY=0 NormalZ=1 AngleXU=2.39375 Radius=1.7
    g102: Circle CenterX=-197.837 CenterY=-70 CenterZ=0 NormalX=0 NormalY=0 NormalZ=1 AngleXU=-1.5708 Radius=1.7
    g103: Circle CenterX=-197.837 CenterY=70 CenterZ=0 NormalX=0 NormalY=0 NormalZ=1 AngleXU=-1.5708 Radius=1.7
    g104: Circle CenterX=-197.837 CenterY=0 CenterZ=0 NormalX=0 NormalY=0 NormalZ=1 AngleXU=-1.5708 Radius=1.7
    g105: Circle CenterX=-227.127 CenterY=441.905 CenterZ=0 NormalX=0 NormalY=0 NormalZ=1 AngleXU=2.39375 Radius=1.7
    g106: Circle CenterX=-196.524 CenterY=474.897 CenterZ=0 NormalX=0 NormalY=0 NormalZ=1 AngleXU=2.39375 Radius=1.7
    g107: Circle CenterX=-196.524 CenterY=-474.897 CenterZ=0 NormalX=0 NormalY=0 NormalZ=1 AngleXU=-2.39375 Radius=1.7
    g108: Circle CenterX=-227.127 CenterY=-441.905 CenterZ=0 NormalX=0 NormalY=0 NormalZ=1 AngleXU=-2.39375 Radius=1.7
    g109: LineSegment StartX=-235.515 StartY=-443.896 StartZ=0 EndX=-234.221 EndY=-442.37 EndZ=0
    g110: LineSegment StartX=-3.94011 StartY=-170.749 StartZ=0 EndX=-5.23346 EndY=-172.274 EndZ=0
    g111: LineSegment StartX=1.08142 StartY=-157.191 StartZ=0 EndX=1.08142 EndY=-155.191 EndZ=0
    g112: LineSegment StartX=1.08142 StartY=157.191 StartZ=0 EndX=1.08142 EndY=155.191 EndZ=0
    g113: LineSegment StartX=-3.94011 StartY=170.749 StartZ=0 EndX=-5.23346 EndY=172.274 EndZ=0
    g114: LineSegment StartX=-235.515 StartY=443.896 StartZ=0 EndX=-234.221 EndY=442.37 EndZ=0
  constraints (108):
    c: Coincident(g109,g-3)
    c: PointOnObject(g109,g-3)
    c: Coincident(g110,g-3)
    c: PointOnObject(g110,g-3)
    c: Coincident(g111,g-4)
    c: PointOnObject(g111,g-4)
    c: Coincident(g112,g-5)
    c: PointOnObject(g112,g-5)
    c: Coincident(g113,g-6)
    c: PointOnObject(g113,g-6)
    c: Coincident(g114,g-6)
    c: PointOnObject(g114,g-6)
    c: Equal(g114,g113)
    c: Equal(g113,g112)
    c: Equal(g112,g111)
    c: Equal(g111,g110)
    c: Equal(g110,g109)
    c: DistanceY(g111,g111) = 2
    c: Coincident(g40,g41)
    c: Coincident(g39,g40)
    c: Coincident(g0,g41)
    c: Coincident(g38,g39)
    c: Coincident(g0,g1)
    c: Coincident(g37,g38)
    c: Coincident(g1,g2)
    c: Coincident(g36,g37)
    c: Coincident(g3,g4)
    c: Coincident(g34,g35)
    c: Coincident(g2,g3)
    c: Coincident(g35,g36)
    c: Coincident(g4,g5)
    c: Coincident(g33,g34)
    c: Coincident(g5,g6)
    c: Coincident(g32,g33)
    c: Coincident(g6,g7)
    c: Coincident(g31,g32)
    c: Coincident(g43,g44)
    c: Coincident(g44,g45)
    c: Coincident(g42,g43)
    c: Coincident(g45,g46)
    c: Coincident(g42,g49)
    c: Coincident(g46,g47)
    c: Coincident(g48,g49)
    c: Coincident(g47,g48)
    c: Coincident(g12,g13)
    c: Coincident(g25,g26)
    c: Coincident(g56,g57)
    c: Coincident(g50,g57)
    c: Coincident(g64,g65)
    c: Coincident(g58,g65)
    c: Coincident(g80,g81)
    c: Coincident(g74,g81)
    c: Coincident(g72,g73)
    c: Coincident(g66,g73)
    c: Coincident(g88,g89)
    c: Coincident(g82,g89)
    c: Coincident(g11,g12)
    c: Coincident(g26,g27)
    c: Coincident(g13,g14)
    c: Coincident(g55,g56)
    c: Coincident(g50,g51)
    c: Coincident(g63,g64)
    c: Coincident(g58,g59)
    c: Coincident(g79,g80)
    c: Coincident(g74,g75)
    c: Coincident(g71,g72)
    c: Coincident(g66,g67)
    c: Coincident(g87,g88)
    c: Coincident(g82,g83)
    c: Coincident(g24,g25)
    c: Coincident(g14,g15)
    c: Coincident(g54,g55)
    c: Coincident(g51,g52)
    c: Coincident(g62,g63)
    c: Coincident(g59,g60)
    c: Coincident(g78,g79)
    c: Coincident(g75,g76)
    c: Coincident(g70,g71)
    c: Coincident(g67,g68)
    c: Coincident(g86,g87)
    c: Coincident(g83,g84)
    c: Coincident(g23,g24)
    c: Coincident(g10,g11)
    c: Coincident(g27,g28)
    c: Coincident(g53,g54)
    c: Coincident(g52,g53)
    c: Coincident(g61,g62)
    c: Coincident(g60,g61)
    c: Coincident(g77,g78)
    c: Coincident(g76,g77)
    c: Coincident(g69,g70)
    c: Coincident(g68,g69)
    c: Coincident(g85,g86)
    c: Coincident(g84,g85)
    c: Coincident(g9,g10)
    c: Coincident(g28,g29)
    c: Coincident(g15,g16)
    c: Coincident(g22,g23)
    c: Coincident(g16,g17)
    c: Coincident(g21,g22)
    c: Coincident(g7,g8)
    c: Coincident(g30,g31)
    c: Coincident(g8,g9)
    c: Coincident(g29,g30)
    c: Coincident(g17,g18)
    c: Coincident(g20,g21)
    c: Coincident(g18,g19)
    c: Coincident(g19,g20)
FEATURE [TechDraw::DrawViewDimension] Dimension019
  AngleOverride = false
  Arbitrary = false
  ArbitraryTolerances = false
  BoxCorners = (2) [(-60,-24.8716,-1e-07),(60,24.8716,1e-07)]
  EqualTolerance = true
  ExtensionAngle = 0
  FormatSpec = %.2w
  FormatSpecOverTolerance = %+.2w
  FormatSpecUnderTolerance = %+.2w
  Inverted = false
  LineAngle = 0
  LockPosition = false
  MeasureType = 1
  OverTolerance = 0
  References2D = -> [View003]
  Rotation = 0
  ScaleType = 0
  TheoreticalExact = false
  Type = 6
  UnderTolerance = 0
  X = -48.7851
  Y = -9.83103
FEATURE [TechDraw::DrawViewDimension] Dimension022
  AngleOverride = false
  Arbitrary = false
  ArbitraryTolerances = false
  BoxCorners = (2) [(-114.687,-29.2611,0),(114.687,29.2611,0)]
  EqualTolerance = true
  ExtensionAngle = 0
  FormatSpec = %.2w
  FormatSpecOverTolerance = %+.2w
  FormatSpecUnderTolerance = %+.2w
  Inverted = false
  LineAngle = 0
  LockPosition = false
  MeasureType = 1
  OverTolerance = 0
  References2D = -> [View002]
  Rotation = 0
  ScaleType = 0
  TheoreticalExact = false
  Type = 6
  UnderTolerance = 0
  X = -104.334
  Y = -12.7469
FEATURE [TechDraw::DrawViewDimension] Dimension024
  AngleOverride = false
  Arbitrary = false
  ArbitraryTolerances = false
  BoxCorners = (2) [(-60,-24.8716,-1e-07),(60,24.8716,1e-07)]
  EqualTolerance = true
  ExtensionAngle = 0
  FormatSpec = %.2w
  FormatSpecOverTolerance = %+.2w
  FormatSpecUnderTolerance = %+.2w
  Inverted = false
  LineAngle = 0
  LockPosition = false
  MeasureType = 1
  OverTolerance = 0
  References2D = -> [View003]
  Rotation = 0
  ScaleType = 0
  TheoreticalExact = false
  Type = 2
  UnderTolerance = 0
  X = 67.4927
  Y = -5.27657
FEATURE [TechDraw::DrawViewBalloon] Balloon
  BubbleShape = 3
  EndType = 0
  EndTypeScale = 1
  KinkLength = 5
  LockPosition = false
  OriginX = 78.1383
  OriginY = 31.4195
  Rotation = 0
  ScaleType = 0
  ShapeScale = 1
  SourceView = -> View004
  Text = Лицевая сторона
  TextWrapLen = -1
  X = 241.673
  Y = 137.439
FEATURE [TechDraw::DrawViewBalloon] Balloon001
  BubbleShape = 3
  EndType = 0
  EndTypeScale = 1
  KinkLength = 5
  LockPosition = false
  OriginX = 129.696
  OriginY = -24.6198
  Rotation = 0
  ScaleType = 0
  ShapeScale = 1
  SourceView = -> View004
  Text = Оборотная сторона
  TextWrapLen = -1
  X = 314.912
  Y = -69.7763
FEATURE [TechDraw::DrawPage] Page001
  KeepUpdated = true
  NextBalloonIndex = 3
  ProjectionType = 0
  Template = -> Template001
  Views = -> [View002,View003,View004,Dimension019,Dimension022,Dimension024,Balloon,Balloon001]
FEATURE [App::DocumentObjectGroup] Group003  label="sink_Group"
  Group = -> [Page001,Unfold006,Unfold_Sketch006,Unfold_Sketch_Outline006,Unfold_Sketch_Internal006,Unfold_Sketch_bends004]
FEATURE [App::DocumentObjectGroup] Group001  label="unfolds"
  Group = -> [Group002,Group004,Group003,Group005,Group007,Group006]
note: 4 file-system paths scrubbed to <path> (originals preserved in the JSON sidecar)

RESOLVED EXTERNAL PARTS (link-assembly join: the EXTERNAL_REF files above that resolve inside this repo's crawl, each included once):
---- part composit_stand12.FCStd = doc fcstd_02e919d733df (291737 chars; too large to inline — full recipe in that document) ----
